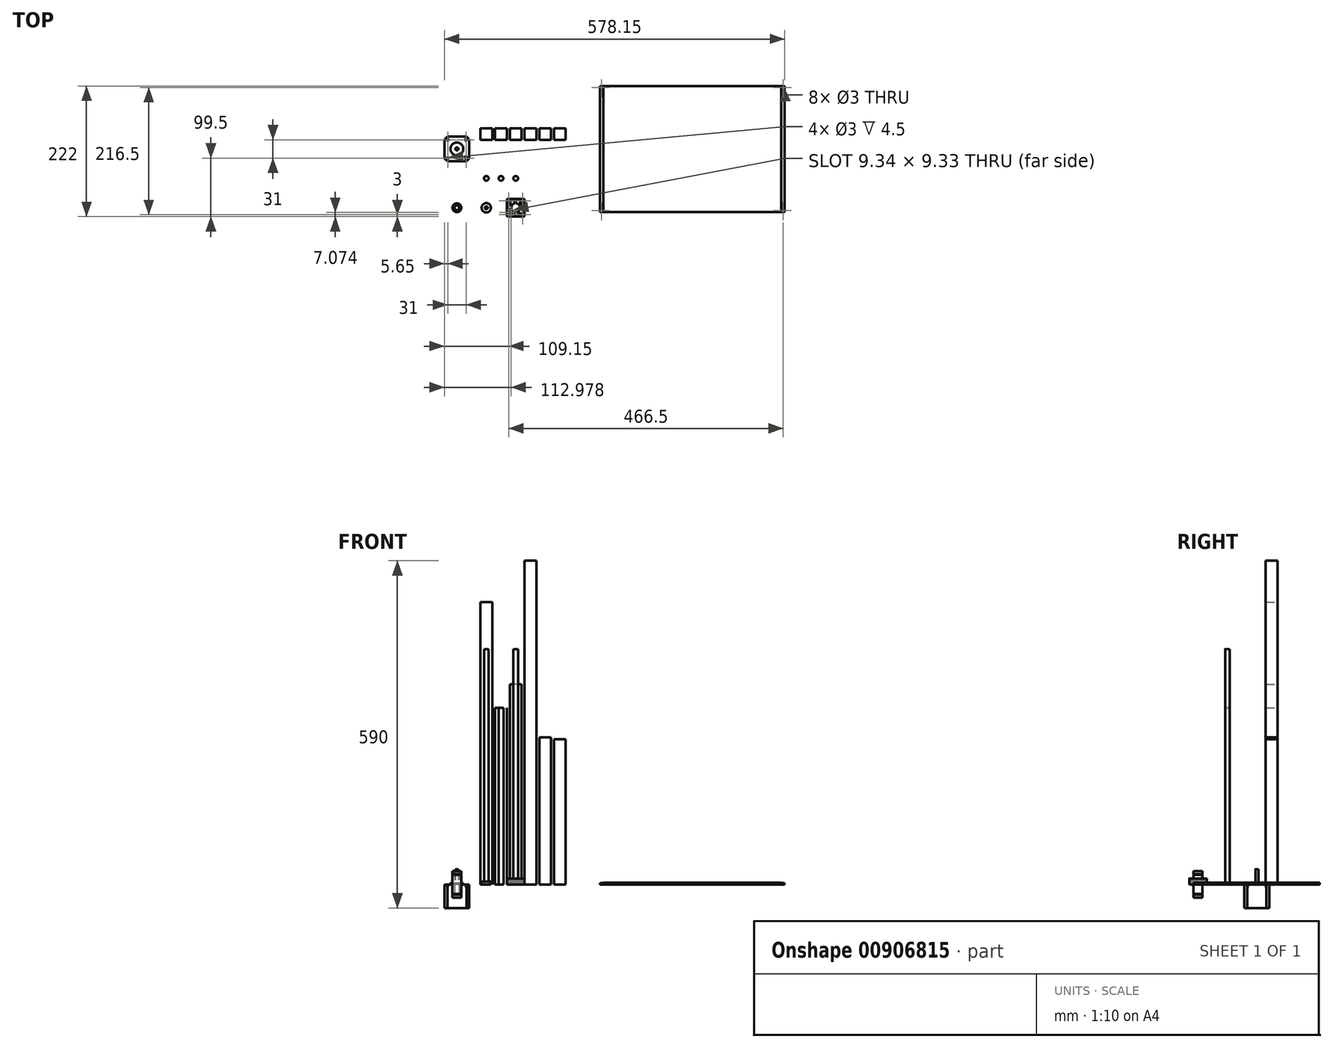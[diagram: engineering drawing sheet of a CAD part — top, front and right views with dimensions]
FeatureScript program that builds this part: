
annotation { "Feature Type Name" : "Feature", "Feature Type Description" : "" }
export const myFeature = defineFeature(function(context is Context, id is Id, definition is map)
    precondition{}
    {
        {
            assignVariable(context, id + "F0", {"name" : "X", "anyValue" : 480});
        }
        {
            assignVariable(context, id + "F1", {"name" : "Y", "anyValue" : 300});
        }
        {
            assignVariable(context, id + "F2", {"name" : "Z", "anyValue" : 550});
        }
        {
            var Q0;
            Q0=qCreatedBy(makeId("Top.planeOp"),FACE);
            var sketch = newSketch(context, id + "F3", { "sketchPlane" : qUnion([Q0])});
            skLineSegment(sketch, "E0.bottom", {"start": v(8.5, -10) * mm, "end": v(-8.5, -10) * mm});
            skLineSegment(sketch, "E0.top", {"start": v(8.5, 10) * mm, "end": v(-8.5, 10) * mm});
            skLineSegment(sketch, "E0.left", {"start": v(10, -8.5) * mm, "end": v(10, 8.5) * mm});
            skLineSegment(sketch, "E0.right", {"start": v(-10, -8.5) * mm, "end": v(-10, 8.5) * mm});
            skPoint(sketch, "E0.middle", {"position": v(0, 0) * mm});
            skPoint(sketch, "E1.visualSharp", {"position": v(-10, 10) * mm});
            skArc(sketch, "E1.filletArc", {"start": v(-8.5, 10) * mm, "mid": v(-9.56, 9.56) * mm, "end": v(-10, 8.5) * mm});
            skPoint(sketch, "E2.visualSharp", {"position": v(10, 10) * mm});
            skArc(sketch, "E2.filletArc", {"start": v(10, 8.5) * mm, "mid": v(9.56, 9.56) * mm, "end": v(8.5, 10) * mm});
            skPoint(sketch, "E3.visualSharp", {"position": v(10, -10) * mm});
            skArc(sketch, "E3.filletArc", {"start": v(8.5, -10) * mm, "mid": v(9.56, -9.56) * mm, "end": v(10, -8.5) * mm});
            skPoint(sketch, "E4.visualSharp", {"position": v(-10, -10) * mm});
            skArc(sketch, "E4.filletArc", {"start": v(-10, -8.5) * mm, "mid": v(-9.56, -9.56) * mm, "end": v(-8.5, -10) * mm});
            skCircle(sketch, "E5", {"center": v(0, 0) * mm, "radius": 2.5 * mm});
            skLineSegment(sketch, "E6", {"start": v(-3.6, -10) * mm, "end": v(-3.6, -9.7) * mm});
            skLineSegment(sketch, "E7", {"start": v(-3.4, -9.5) * mm, "end": v(-3.1, -9.5) * mm});
            skLineSegment(sketch, "E8", {"start": v(-3.1, -9.5) * mm, "end": v(-3.1, -8.2) * mm});
            skLineSegment(sketch, "E9", {"start": v(-3.1, -8.2) * mm, "end": v(-5.5, -8.2) * mm});
            skLineSegment(sketch, "E10", {"start": v(-3.43, -4.49) * mm, "end": v(-5.5, -6.56) * mm});
            skLineSegment(sketch, "E11", {"start": v(-2.01, -3.9) * mm, "end": v(2.01, -3.9) * mm});
            skLineSegment(sketch, "E12", {"start": v(5.5, -6.56) * mm, "end": v(3.43, -4.49) * mm});
            skLineSegment(sketch, "E13", {"start": v(5.5, -8.2) * mm, "end": v(3.1, -8.2) * mm});
            skLineSegment(sketch, "E14", {"start": v(3.1, -8.2) * mm, "end": v(3.1, -9.5) * mm});
            skLineSegment(sketch, "E15", {"start": v(3.1, -9.5) * mm, "end": v(3.4, -9.5) * mm});
            skLineSegment(sketch, "E16", {"start": v(3.6, -9.7) * mm, "end": v(3.6, -10) * mm});
            skLineSegment(sketch, "E17", {"start": v(0, 0) * mm, "end": v(0, -10) * mm, "construction": true});
            skLineSegment(sketch, "E18", {"start": v(5.5, -6.56) * mm, "end": v(5.5, -8.2) * mm});
            skLineSegment(sketch, "E19", {"start": v(-5.5, -6.56) * mm, "end": v(-5.5, -8.2) * mm});
            skPoint(sketch, "E20.visualSharp", {"position": v(-2.84, -3.9) * mm});
            skArc(sketch, "E20.filletArc", {"start": v(-2.01, -3.9) * mm, "mid": v(-2.78, -4.05) * mm, "end": v(-3.43, -4.49) * mm});
            skPoint(sketch, "E21.visualSharp", {"position": v(2.84, -3.9) * mm});
            skArc(sketch, "E21.filletArc", {"start": v(3.43, -4.49) * mm, "mid": v(2.78, -4.05) * mm, "end": v(2.01, -3.9) * mm});
            skPoint(sketch, "E22.visualSharp", {"position": v(-3.6, -9.5) * mm});
            skArc(sketch, "E22.filletArc", {"start": v(-3.4, -9.5) * mm, "mid": v(-3.54, -9.56) * mm, "end": v(-3.6, -9.7) * mm});
            skPoint(sketch, "E23.visualSharp", {"position": v(3.6, -9.5) * mm});
            skArc(sketch, "E23.filletArc", {"start": v(3.6, -9.7) * mm, "mid": v(3.54, -9.56) * mm, "end": v(3.4, -9.5) * mm});
            skLineSegment(sketch, "E24.1.0", {"start": v(6.56, 5.5) * mm, "end": v(4.49, 3.43) * mm});
            skLineSegment(sketch, "E24.1.1", {"start": v(3.9, -2.01) * mm, "end": v(3.9, 2.01) * mm});
            skLineSegment(sketch, "E24.1.2", {"start": v(6.56, 5.5) * mm, "end": v(8.2, 5.5) * mm});
            skArc(sketch, "E24.1.3", {"start": v(4.49, 3.43) * mm, "mid": v(4.05, 2.78) * mm, "end": v(3.9, 2.01) * mm});
            skLineSegment(sketch, "E24.1.4", {"start": v(8.2, 3.1) * mm, "end": v(9.5, 3.1) * mm});
            skPoint(sketch, "E24.1.5", {"position": v(3.9, -2.84) * mm});
            skPoint(sketch, "E24.1.6", {"position": v(9.5, -3.6) * mm});
            skPoint(sketch, "E24.1.7", {"position": v(9.5, 3.6) * mm});
            skLineSegment(sketch, "E24.1.8", {"start": v(8.2, -3.1) * mm, "end": v(8.2, -5.5) * mm});
            skLineSegment(sketch, "E24.1.9", {"start": v(9.7, 3.6) * mm, "end": v(10, 3.6) * mm});
            skLineSegment(sketch, "E24.1.10", {"start": v(9.5, -3.1) * mm, "end": v(8.2, -3.1) * mm});
            skLineSegment(sketch, "E24.1.11", {"start": v(8.2, 5.5) * mm, "end": v(8.2, 3.1) * mm});
            skLineSegment(sketch, "E24.1.12", {"start": v(4.49, -3.43) * mm, "end": v(6.56, -5.5) * mm});
            skPoint(sketch, "E24.1.13", {"position": v(3.9, 2.84) * mm});
            skLineSegment(sketch, "E24.1.14", {"start": v(6.56, -5.5) * mm, "end": v(8.2, -5.5) * mm});
            skLineSegment(sketch, "E24.1.15", {"start": v(9.5, 3.1) * mm, "end": v(9.5, 3.4) * mm});
            skLineSegment(sketch, "E24.1.16", {"start": v(9.5, -3.4) * mm, "end": v(9.5, -3.1) * mm});
            skArc(sketch, "E24.1.17", {"start": v(3.9, -2.01) * mm, "mid": v(4.05, -2.78) * mm, "end": v(4.49, -3.43) * mm});
            skLineSegment(sketch, "E24.1.18", {"start": v(10, -3.6) * mm, "end": v(9.7, -3.6) * mm});
            skArc(sketch, "E24.1.19", {"start": v(9.5, -3.4) * mm, "mid": v(9.56, -3.54) * mm, "end": v(9.7, -3.6) * mm});
            skArc(sketch, "E24.1.20", {"start": v(9.7, 3.6) * mm, "mid": v(9.56, 3.54) * mm, "end": v(9.5, 3.4) * mm});
            skLineSegment(sketch, "E24.2.0", {"start": v(-5.5, 6.56) * mm, "end": v(-3.43, 4.49) * mm});
            skLineSegment(sketch, "E24.2.1", {"start": v(2.01, 3.9) * mm, "end": v(-2.01, 3.9) * mm});
            skLineSegment(sketch, "E24.2.2", {"start": v(-5.5, 6.56) * mm, "end": v(-5.5, 8.2) * mm});
            skArc(sketch, "E24.2.3", {"start": v(-3.43, 4.49) * mm, "mid": v(-2.78, 4.05) * mm, "end": v(-2.01, 3.9) * mm});
            skLineSegment(sketch, "E24.2.4", {"start": v(-3.1, 8.2) * mm, "end": v(-3.1, 9.5) * mm});
            skPoint(sketch, "E24.2.5", {"position": v(2.84, 3.9) * mm});
            skPoint(sketch, "E24.2.6", {"position": v(3.6, 9.5) * mm});
            skPoint(sketch, "E24.2.7", {"position": v(-3.6, 9.5) * mm});
            skLineSegment(sketch, "E24.2.8", {"start": v(3.1, 8.2) * mm, "end": v(5.5, 8.2) * mm});
            skLineSegment(sketch, "E24.2.9", {"start": v(-3.6, 9.7) * mm, "end": v(-3.6, 10) * mm});
            skLineSegment(sketch, "E24.2.10", {"start": v(3.1, 9.5) * mm, "end": v(3.1, 8.2) * mm});
            skLineSegment(sketch, "E24.2.11", {"start": v(-5.5, 8.2) * mm, "end": v(-3.1, 8.2) * mm});
            skLineSegment(sketch, "E24.2.12", {"start": v(3.43, 4.49) * mm, "end": v(5.5, 6.56) * mm});
            skPoint(sketch, "E24.2.13", {"position": v(-2.84, 3.9) * mm});
            skLineSegment(sketch, "E24.2.14", {"start": v(5.5, 6.56) * mm, "end": v(5.5, 8.2) * mm});
            skLineSegment(sketch, "E24.2.15", {"start": v(-3.1, 9.5) * mm, "end": v(-3.4, 9.5) * mm});
            skLineSegment(sketch, "E24.2.16", {"start": v(3.4, 9.5) * mm, "end": v(3.1, 9.5) * mm});
            skArc(sketch, "E24.2.17", {"start": v(2.01, 3.9) * mm, "mid": v(2.78, 4.05) * mm, "end": v(3.43, 4.49) * mm});
            skLineSegment(sketch, "E24.2.18", {"start": v(3.6, 10) * mm, "end": v(3.6, 9.7) * mm});
            skArc(sketch, "E24.2.19", {"start": v(3.4, 9.5) * mm, "mid": v(3.54, 9.56) * mm, "end": v(3.6, 9.7) * mm});
            skArc(sketch, "E24.2.20", {"start": v(-3.6, 9.7) * mm, "mid": v(-3.54, 9.56) * mm, "end": v(-3.4, 9.5) * mm});
            skLineSegment(sketch, "E24.3.0", {"start": v(-6.56, -5.5) * mm, "end": v(-4.49, -3.43) * mm});
            skLineSegment(sketch, "E24.3.1", {"start": v(-3.9, 2.01) * mm, "end": v(-3.9, -2.01) * mm});
            skLineSegment(sketch, "E24.3.2", {"start": v(-6.56, -5.5) * mm, "end": v(-8.2, -5.5) * mm});
            skArc(sketch, "E24.3.3", {"start": v(-4.49, -3.43) * mm, "mid": v(-4.05, -2.78) * mm, "end": v(-3.9, -2.01) * mm});
            skLineSegment(sketch, "E24.3.4", {"start": v(-8.2, -3.1) * mm, "end": v(-9.5, -3.1) * mm});
            skPoint(sketch, "E24.3.5", {"position": v(-3.9, 2.84) * mm});
            skPoint(sketch, "E24.3.6", {"position": v(-9.5, 3.6) * mm});
            skPoint(sketch, "E24.3.7", {"position": v(-9.5, -3.6) * mm});
            skLineSegment(sketch, "E24.3.8", {"start": v(-8.2, 3.1) * mm, "end": v(-8.2, 5.5) * mm});
            skLineSegment(sketch, "E24.3.9", {"start": v(-9.7, -3.6) * mm, "end": v(-10, -3.6) * mm});
            skLineSegment(sketch, "E24.3.10", {"start": v(-9.5, 3.1) * mm, "end": v(-8.2, 3.1) * mm});
            skLineSegment(sketch, "E24.3.11", {"start": v(-8.2, -5.5) * mm, "end": v(-8.2, -3.1) * mm});
            skLineSegment(sketch, "E24.3.12", {"start": v(-4.49, 3.43) * mm, "end": v(-6.56, 5.5) * mm});
            skPoint(sketch, "E24.3.13", {"position": v(-3.9, -2.84) * mm});
            skLineSegment(sketch, "E24.3.14", {"start": v(-6.56, 5.5) * mm, "end": v(-8.2, 5.5) * mm});
            skLineSegment(sketch, "E24.3.15", {"start": v(-9.5, -3.1) * mm, "end": v(-9.5, -3.4) * mm});
            skLineSegment(sketch, "E24.3.16", {"start": v(-9.5, 3.4) * mm, "end": v(-9.5, 3.1) * mm});
            skArc(sketch, "E24.3.17", {"start": v(-3.9, 2.01) * mm, "mid": v(-4.05, 2.78) * mm, "end": v(-4.49, 3.43) * mm});
            skLineSegment(sketch, "E24.3.18", {"start": v(-10, 3.6) * mm, "end": v(-9.7, 3.6) * mm});
            skArc(sketch, "E24.3.19", {"start": v(-9.5, 3.4) * mm, "mid": v(-9.56, 3.54) * mm, "end": v(-9.7, 3.6) * mm});
            skArc(sketch, "E24.3.20", {"start": v(-9.7, -3.6) * mm, "mid": v(-9.56, -3.54) * mm, "end": v(-9.5, -3.4) * mm});
            skLineSegment(sketch, "E25.1.0.0", {"start": v(33.5, 10) * mm, "end": v(16.5, 10) * mm});
            skLineSegment(sketch, "E25.1.0.1", {"start": v(35, -8.5) * mm, "end": v(35, 8.5) * mm});
            skLineSegment(sketch, "E25.1.0.2", {"start": v(33.5, -10) * mm, "end": v(16.5, -10) * mm});
            skLineSegment(sketch, "E25.1.0.3", {"start": v(30.5, -6.56) * mm, "end": v(28.43, -4.49) * mm});
            skLineSegment(sketch, "E25.1.0.4", {"start": v(15, -8.5) * mm, "end": v(15, 8.5) * mm});
            skPoint(sketch, "E25.1.0.5", {"position": v(15, 10) * mm});
            skPoint(sketch, "E25.1.0.6", {"position": v(35, -10) * mm});
            skCircle(sketch, "E25.1.0.7", {"center": v(25, 0) * mm, "radius": 2.5 * mm});
            skLineSegment(sketch, "E25.1.0.8", {"start": v(28.1, 8.2) * mm, "end": v(30.5, 8.2) * mm});
            skPoint(sketch, "E25.1.0.9", {"position": v(21.1, -2.84) * mm});
            skPoint(sketch, "E25.1.0.10", {"position": v(28.9, 2.84) * mm});
            skLineSegment(sketch, "E25.1.0.11", {"start": v(18.44, -5.5) * mm, "end": v(20.51, -3.43) * mm});
            skLineSegment(sketch, "E25.1.0.12", {"start": v(30.5, -8.2) * mm, "end": v(28.1, -8.2) * mm});
            skPoint(sketch, "E25.1.0.13", {"position": v(15, -10) * mm});
            skLineSegment(sketch, "E25.1.0.14", {"start": v(22.99, -3.9) * mm, "end": v(27.01, -3.9) * mm});
            skLineSegment(sketch, "E25.1.0.15", {"start": v(27.01, 3.9) * mm, "end": v(22.99, 3.9) * mm});
            skLineSegment(sketch, "E25.1.0.16", {"start": v(31.56, 5.5) * mm, "end": v(29.49, 3.43) * mm});
            skPoint(sketch, "E25.1.0.17", {"position": v(15.5, 3.6) * mm});
            skPoint(sketch, "E25.1.0.18", {"position": v(34.5, -3.6) * mm});
            skLineSegment(sketch, "E25.1.0.19", {"start": v(33.2, -3.1) * mm, "end": v(33.2, -5.5) * mm});
            skLineSegment(sketch, "E25.1.0.20", {"start": v(21.57, -4.49) * mm, "end": v(19.5, -6.56) * mm});
            skPoint(sketch, "E25.1.0.21", {"position": v(15.5, -3.6) * mm});
            skPoint(sketch, "E25.1.0.22", {"position": v(34.5, 3.6) * mm});
            skLineSegment(sketch, "E25.1.0.23", {"start": v(19.5, 6.56) * mm, "end": v(21.57, 4.49) * mm});
            skLineSegment(sketch, "E25.1.0.24", {"start": v(28.9, -2.01) * mm, "end": v(28.9, 2.01) * mm});
            skLineSegment(sketch, "E25.1.0.25", {"start": v(21.1, 2.01) * mm, "end": v(21.1, -2.01) * mm});
            skLineSegment(sketch, "E25.1.0.26", {"start": v(16.8, 3.1) * mm, "end": v(16.8, 5.5) * mm});
            skPoint(sketch, "E25.1.0.27", {"position": v(35, 10) * mm});
            skPoint(sketch, "E25.1.0.28", {"position": v(28.9, -2.84) * mm});
            skPoint(sketch, "E25.1.0.29", {"position": v(21.1, 2.84) * mm});
            skPoint(sketch, "E25.1.0.30", {"position": v(25, 0) * mm});
            skPoint(sketch, "E25.1.0.31", {"position": v(28.6, -9.5) * mm});
            skPoint(sketch, "E25.1.0.32", {"position": v(22.16, 3.9) * mm});
            skPoint(sketch, "E25.1.0.33", {"position": v(21.4, 9.5) * mm});
            skLineSegment(sketch, "E25.1.0.34", {"start": v(20.51, 3.43) * mm, "end": v(18.44, 5.5) * mm});
            skPoint(sketch, "E25.1.0.35", {"position": v(27.84, -3.9) * mm});
            skPoint(sketch, "E25.1.0.36", {"position": v(28.6, 9.5) * mm});
            skLineSegment(sketch, "E25.1.0.37", {"start": v(28.43, 4.49) * mm, "end": v(30.5, 6.56) * mm});
            skLineSegment(sketch, "E25.1.0.38", {"start": v(16.8, -5.5) * mm, "end": v(16.8, -3.1) * mm});
            skPoint(sketch, "E25.1.0.39", {"position": v(27.84, 3.9) * mm});
            skLineSegment(sketch, "E25.1.0.40", {"start": v(29.49, -3.43) * mm, "end": v(31.56, -5.5) * mm});
            skLineSegment(sketch, "E25.1.0.41", {"start": v(19.5, 8.2) * mm, "end": v(21.9, 8.2) * mm});
            skLineSegment(sketch, "E25.1.0.42", {"start": v(25, 0) * mm, "end": v(25, -10) * mm, "construction": true});
            skPoint(sketch, "E25.1.0.43", {"position": v(22.16, -3.9) * mm});
            skLineSegment(sketch, "E25.1.0.44", {"start": v(33.2, 5.5) * mm, "end": v(33.2, 3.1) * mm});
            skArc(sketch, "E25.1.0.45", {"start": v(35, 8.5) * mm, "mid": v(34.56, 9.56) * mm, "end": v(33.5, 10) * mm});
            skArc(sketch, "E25.1.0.46", {"start": v(16.5, 10) * mm, "mid": v(15.44, 9.56) * mm, "end": v(15, 8.5) * mm});
            skLineSegment(sketch, "E25.1.0.47", {"start": v(21.9, -8.2) * mm, "end": v(19.5, -8.2) * mm});
            skArc(sketch, "E25.1.0.48", {"start": v(33.5, -10) * mm, "mid": v(34.56, -9.56) * mm, "end": v(35, -8.5) * mm});
            skArc(sketch, "E25.1.0.49", {"start": v(15, -8.5) * mm, "mid": v(15.44, -9.56) * mm, "end": v(16.5, -10) * mm});
            skPoint(sketch, "E25.1.0.50", {"position": v(21.4, -9.5) * mm});
            skPoint(sketch, "E25.1.0.51", {"position": v(25, 0) * mm});
            skLineSegment(sketch, "E25.1.0.52", {"start": v(28.1, -8.2) * mm, "end": v(28.1, -9.5) * mm});
            skLineSegment(sketch, "E25.1.0.53", {"start": v(16.8, -3.1) * mm, "end": v(15.5, -3.1) * mm});
            skLineSegment(sketch, "E25.1.0.54", {"start": v(18.44, -5.5) * mm, "end": v(16.8, -5.5) * mm});
            skArc(sketch, "E25.1.0.55", {"start": v(20.51, -3.43) * mm, "mid": v(20.95, -2.78) * mm, "end": v(21.1, -2.01) * mm});
            skLineSegment(sketch, "E25.1.0.56", {"start": v(21.9, 8.2) * mm, "end": v(21.9, 9.5) * mm});
            skLineSegment(sketch, "E25.1.0.57", {"start": v(33.2, 3.1) * mm, "end": v(34.5, 3.1) * mm});
            skLineSegment(sketch, "E25.1.0.58", {"start": v(31.56, 5.5) * mm, "end": v(33.2, 5.5) * mm});
            skArc(sketch, "E25.1.0.59", {"start": v(21.57, 4.49) * mm, "mid": v(22.22, 4.05) * mm, "end": v(22.99, 3.9) * mm});
            skLineSegment(sketch, "E25.1.0.60", {"start": v(19.5, 6.56) * mm, "end": v(19.5, 8.2) * mm});
            skLineSegment(sketch, "E25.1.0.61", {"start": v(34.5, -3.1) * mm, "end": v(33.2, -3.1) * mm});
            skArc(sketch, "E25.1.0.62", {"start": v(29.49, 3.43) * mm, "mid": v(29.05, 2.78) * mm, "end": v(28.9, 2.01) * mm});
            skArc(sketch, "E25.1.0.63", {"start": v(21.1, 2.01) * mm, "mid": v(20.95, 2.78) * mm, "end": v(20.51, 3.43) * mm});
            skArc(sketch, "E25.1.0.64", {"start": v(27.01, 3.9) * mm, "mid": v(27.78, 4.05) * mm, "end": v(28.43, 4.49) * mm});
            skArc(sketch, "E25.1.0.65", {"start": v(28.43, -4.49) * mm, "mid": v(27.78, -4.05) * mm, "end": v(27.01, -3.9) * mm});
            skArc(sketch, "E25.1.0.66", {"start": v(28.9, -2.01) * mm, "mid": v(29.05, -2.78) * mm, "end": v(29.49, -3.43) * mm});
            skLineSegment(sketch, "E25.1.0.67", {"start": v(18.44, 5.5) * mm, "end": v(16.8, 5.5) * mm});
            skArc(sketch, "E25.1.0.68", {"start": v(22.99, -3.9) * mm, "mid": v(22.22, -4.05) * mm, "end": v(21.57, -4.49) * mm});
            skLineSegment(sketch, "E25.1.0.69", {"start": v(30.5, 6.56) * mm, "end": v(30.5, 8.2) * mm});
            skLineSegment(sketch, "E25.1.0.70", {"start": v(19.5, -6.56) * mm, "end": v(19.5, -8.2) * mm});
            skLineSegment(sketch, "E25.1.0.71", {"start": v(31.56, -5.5) * mm, "end": v(33.2, -5.5) * mm});
            skLineSegment(sketch, "E25.1.0.72", {"start": v(30.5, -6.56) * mm, "end": v(30.5, -8.2) * mm});
            skLineSegment(sketch, "E25.1.0.73", {"start": v(15.5, 3.1) * mm, "end": v(16.8, 3.1) * mm});
            skLineSegment(sketch, "E25.1.0.74", {"start": v(28.1, 9.5) * mm, "end": v(28.1, 8.2) * mm});
            skLineSegment(sketch, "E25.1.0.75", {"start": v(21.9, -9.5) * mm, "end": v(21.9, -8.2) * mm});
            skArc(sketch, "E25.1.0.76", {"start": v(34.5, -3.4) * mm, "mid": v(34.56, -3.54) * mm, "end": v(34.7, -3.6) * mm});
            skLineSegment(sketch, "E25.1.0.77", {"start": v(35, -3.6) * mm, "end": v(34.7, -3.6) * mm});
            skLineSegment(sketch, "E25.1.0.78", {"start": v(34.5, -3.4) * mm, "end": v(34.5, -3.1) * mm});
            skArc(sketch, "E25.1.0.79", {"start": v(15.3, -3.6) * mm, "mid": v(15.44, -3.54) * mm, "end": v(15.5, -3.4) * mm});
            skArc(sketch, "E25.1.0.80", {"start": v(28.4, 9.5) * mm, "mid": v(28.54, 9.56) * mm, "end": v(28.6, 9.7) * mm});
            skLineSegment(sketch, "E25.1.0.81", {"start": v(28.1, -9.5) * mm, "end": v(28.4, -9.5) * mm});
            skArc(sketch, "E25.1.0.82", {"start": v(28.6, -9.7) * mm, "mid": v(28.54, -9.56) * mm, "end": v(28.4, -9.5) * mm});
            skLineSegment(sketch, "E25.1.0.83", {"start": v(28.6, 10) * mm, "end": v(28.6, 9.7) * mm});
            skLineSegment(sketch, "E25.1.0.84", {"start": v(15.5, -3.1) * mm, "end": v(15.5, -3.4) * mm});
            skLineSegment(sketch, "E25.1.0.85", {"start": v(28.4, 9.5) * mm, "end": v(28.1, 9.5) * mm});
            skLineSegment(sketch, "E25.1.0.86", {"start": v(15.3, -3.6) * mm, "end": v(15, -3.6) * mm});
            skLineSegment(sketch, "E25.1.0.87", {"start": v(28.6, -9.7) * mm, "end": v(28.6, -10) * mm});
            skArc(sketch, "E25.1.0.88", {"start": v(21.4, 9.7) * mm, "mid": v(21.46, 9.56) * mm, "end": v(21.6, 9.5) * mm});
            skLineSegment(sketch, "E25.1.0.89", {"start": v(21.4, -10) * mm, "end": v(21.4, -9.7) * mm});
            skLineSegment(sketch, "E25.1.0.90", {"start": v(21.6, -9.5) * mm, "end": v(21.9, -9.5) * mm});
            skLineSegment(sketch, "E25.1.0.91", {"start": v(21.4, 9.7) * mm, "end": v(21.4, 10) * mm});
            skLineSegment(sketch, "E25.1.0.92", {"start": v(21.9, 9.5) * mm, "end": v(21.6, 9.5) * mm});
            skLineSegment(sketch, "E25.1.0.93", {"start": v(15, 3.6) * mm, "end": v(15.3, 3.6) * mm});
            skArc(sketch, "E25.1.0.94", {"start": v(34.7, 3.6) * mm, "mid": v(34.56, 3.54) * mm, "end": v(34.5, 3.4) * mm});
            skArc(sketch, "E25.1.0.95", {"start": v(15.5, 3.4) * mm, "mid": v(15.44, 3.54) * mm, "end": v(15.3, 3.6) * mm});
            skLineSegment(sketch, "E25.1.0.96", {"start": v(34.7, 3.6) * mm, "end": v(35, 3.6) * mm});
            skLineSegment(sketch, "E25.1.0.97", {"start": v(15.5, 3.4) * mm, "end": v(15.5, 3.1) * mm});
            skArc(sketch, "E25.1.0.98", {"start": v(21.6, -9.5) * mm, "mid": v(21.46, -9.56) * mm, "end": v(21.4, -9.7) * mm});
            skLineSegment(sketch, "E25.1.0.99", {"start": v(34.5, 3.1) * mm, "end": v(34.5, 3.4) * mm});
            skLineSegment(sketch, "E25.2.0.0", {"start": v(58.5, 10) * mm, "end": v(41.5, 10) * mm});
            skLineSegment(sketch, "E25.2.0.1", {"start": v(60, -8.5) * mm, "end": v(60, 8.5) * mm});
            skLineSegment(sketch, "E25.2.0.2", {"start": v(58.5, -10) * mm, "end": v(41.5, -10) * mm});
            skLineSegment(sketch, "E25.2.0.3", {"start": v(55.5, -6.56) * mm, "end": v(53.43, -4.49) * mm});
            skLineSegment(sketch, "E25.2.0.4", {"start": v(40, -8.5) * mm, "end": v(40, 8.5) * mm});
            skPoint(sketch, "E25.2.0.5", {"position": v(40, 10) * mm});
            skPoint(sketch, "E25.2.0.6", {"position": v(60, -10) * mm});
            skCircle(sketch, "E25.2.0.7", {"center": v(50, 0) * mm, "radius": 2.5 * mm});
            skLineSegment(sketch, "E25.2.0.8", {"start": v(53.1, 8.2) * mm, "end": v(55.5, 8.2) * mm});
            skPoint(sketch, "E25.2.0.9", {"position": v(46.1, -2.84) * mm});
            skPoint(sketch, "E25.2.0.10", {"position": v(53.9, 2.84) * mm});
            skLineSegment(sketch, "E25.2.0.11", {"start": v(43.44, -5.5) * mm, "end": v(45.51, -3.43) * mm});
            skLineSegment(sketch, "E25.2.0.12", {"start": v(55.5, -8.2) * mm, "end": v(53.1, -8.2) * mm});
            skPoint(sketch, "E25.2.0.13", {"position": v(40, -10) * mm});
            skLineSegment(sketch, "E25.2.0.14", {"start": v(47.99, -3.9) * mm, "end": v(52.01, -3.9) * mm});
            skLineSegment(sketch, "E25.2.0.15", {"start": v(52.01, 3.9) * mm, "end": v(47.99, 3.9) * mm});
            skLineSegment(sketch, "E25.2.0.16", {"start": v(56.56, 5.5) * mm, "end": v(54.49, 3.43) * mm});
            skPoint(sketch, "E25.2.0.17", {"position": v(40.5, 3.6) * mm});
            skPoint(sketch, "E25.2.0.18", {"position": v(59.5, -3.6) * mm});
            skLineSegment(sketch, "E25.2.0.19", {"start": v(58.2, -3.1) * mm, "end": v(58.2, -5.5) * mm});
            skLineSegment(sketch, "E25.2.0.20", {"start": v(46.57, -4.49) * mm, "end": v(44.5, -6.56) * mm});
            skPoint(sketch, "E25.2.0.21", {"position": v(40.5, -3.6) * mm});
            skPoint(sketch, "E25.2.0.22", {"position": v(59.5, 3.6) * mm});
            skLineSegment(sketch, "E25.2.0.23", {"start": v(44.5, 6.56) * mm, "end": v(46.57, 4.49) * mm});
            skLineSegment(sketch, "E25.2.0.24", {"start": v(53.9, -2.01) * mm, "end": v(53.9, 2.01) * mm});
            skLineSegment(sketch, "E25.2.0.25", {"start": v(46.1, 2.01) * mm, "end": v(46.1, -2.01) * mm});
            skLineSegment(sketch, "E25.2.0.26", {"start": v(41.8, 3.1) * mm, "end": v(41.8, 5.5) * mm});
            skPoint(sketch, "E25.2.0.27", {"position": v(60, 10) * mm});
            skPoint(sketch, "E25.2.0.28", {"position": v(53.9, -2.84) * mm});
            skPoint(sketch, "E25.2.0.29", {"position": v(46.1, 2.84) * mm});
            skPoint(sketch, "E25.2.0.30", {"position": v(50, 0) * mm});
            skPoint(sketch, "E25.2.0.31", {"position": v(53.6, -9.5) * mm});
            skPoint(sketch, "E25.2.0.32", {"position": v(47.16, 3.9) * mm});
            skPoint(sketch, "E25.2.0.33", {"position": v(46.4, 9.5) * mm});
            skLineSegment(sketch, "E25.2.0.34", {"start": v(45.51, 3.43) * mm, "end": v(43.44, 5.5) * mm});
            skPoint(sketch, "E25.2.0.35", {"position": v(52.84, -3.9) * mm});
            skPoint(sketch, "E25.2.0.36", {"position": v(53.6, 9.5) * mm});
            skLineSegment(sketch, "E25.2.0.37", {"start": v(53.43, 4.49) * mm, "end": v(55.5, 6.56) * mm});
            skLineSegment(sketch, "E25.2.0.38", {"start": v(41.8, -5.5) * mm, "end": v(41.8, -3.1) * mm});
            skPoint(sketch, "E25.2.0.39", {"position": v(52.84, 3.9) * mm});
            skLineSegment(sketch, "E25.2.0.40", {"start": v(54.49, -3.43) * mm, "end": v(56.56, -5.5) * mm});
            skLineSegment(sketch, "E25.2.0.41", {"start": v(44.5, 8.2) * mm, "end": v(46.9, 8.2) * mm});
            skLineSegment(sketch, "E25.2.0.42", {"start": v(50, 0) * mm, "end": v(50, -10) * mm, "construction": true});
            skPoint(sketch, "E25.2.0.43", {"position": v(47.16, -3.9) * mm});
            skLineSegment(sketch, "E25.2.0.44", {"start": v(58.2, 5.5) * mm, "end": v(58.2, 3.1) * mm});
            skArc(sketch, "E25.2.0.45", {"start": v(60, 8.5) * mm, "mid": v(59.56, 9.56) * mm, "end": v(58.5, 10) * mm});
            skArc(sketch, "E25.2.0.46", {"start": v(41.5, 10) * mm, "mid": v(40.44, 9.56) * mm, "end": v(40, 8.5) * mm});
            skLineSegment(sketch, "E25.2.0.47", {"start": v(46.9, -8.2) * mm, "end": v(44.5, -8.2) * mm});
            skArc(sketch, "E25.2.0.48", {"start": v(58.5, -10) * mm, "mid": v(59.56, -9.56) * mm, "end": v(60, -8.5) * mm});
            skArc(sketch, "E25.2.0.49", {"start": v(40, -8.5) * mm, "mid": v(40.44, -9.56) * mm, "end": v(41.5, -10) * mm});
            skPoint(sketch, "E25.2.0.50", {"position": v(46.4, -9.5) * mm});
            skPoint(sketch, "E25.2.0.51", {"position": v(50, 0) * mm});
            skLineSegment(sketch, "E25.2.0.52", {"start": v(53.1, -8.2) * mm, "end": v(53.1, -9.5) * mm});
            skLineSegment(sketch, "E25.2.0.53", {"start": v(41.8, -3.1) * mm, "end": v(40.5, -3.1) * mm});
            skLineSegment(sketch, "E25.2.0.54", {"start": v(43.44, -5.5) * mm, "end": v(41.8, -5.5) * mm});
            skArc(sketch, "E25.2.0.55", {"start": v(45.51, -3.43) * mm, "mid": v(45.95, -2.78) * mm, "end": v(46.1, -2.01) * mm});
            skLineSegment(sketch, "E25.2.0.56", {"start": v(46.9, 8.2) * mm, "end": v(46.9, 9.5) * mm});
            skLineSegment(sketch, "E25.2.0.57", {"start": v(58.2, 3.1) * mm, "end": v(59.5, 3.1) * mm});
            skLineSegment(sketch, "E25.2.0.58", {"start": v(56.56, 5.5) * mm, "end": v(58.2, 5.5) * mm});
            skArc(sketch, "E25.2.0.59", {"start": v(46.57, 4.49) * mm, "mid": v(47.22, 4.05) * mm, "end": v(47.99, 3.9) * mm});
            skLineSegment(sketch, "E25.2.0.60", {"start": v(44.5, 6.56) * mm, "end": v(44.5, 8.2) * mm});
            skLineSegment(sketch, "E25.2.0.61", {"start": v(59.5, -3.1) * mm, "end": v(58.2, -3.1) * mm});
            skArc(sketch, "E25.2.0.62", {"start": v(54.49, 3.43) * mm, "mid": v(54.05, 2.78) * mm, "end": v(53.9, 2.01) * mm});
            skArc(sketch, "E25.2.0.63", {"start": v(46.1, 2.01) * mm, "mid": v(45.95, 2.78) * mm, "end": v(45.51, 3.43) * mm});
            skArc(sketch, "E25.2.0.64", {"start": v(52.01, 3.9) * mm, "mid": v(52.78, 4.05) * mm, "end": v(53.43, 4.49) * mm});
            skArc(sketch, "E25.2.0.65", {"start": v(53.43, -4.49) * mm, "mid": v(52.78, -4.05) * mm, "end": v(52.01, -3.9) * mm});
            skArc(sketch, "E25.2.0.66", {"start": v(53.9, -2.01) * mm, "mid": v(54.05, -2.78) * mm, "end": v(54.49, -3.43) * mm});
            skLineSegment(sketch, "E25.2.0.67", {"start": v(43.44, 5.5) * mm, "end": v(41.8, 5.5) * mm});
            skArc(sketch, "E25.2.0.68", {"start": v(47.99, -3.9) * mm, "mid": v(47.22, -4.05) * mm, "end": v(46.57, -4.49) * mm});
            skLineSegment(sketch, "E25.2.0.69", {"start": v(55.5, 6.56) * mm, "end": v(55.5, 8.2) * mm});
            skLineSegment(sketch, "E25.2.0.70", {"start": v(44.5, -6.56) * mm, "end": v(44.5, -8.2) * mm});
            skLineSegment(sketch, "E25.2.0.71", {"start": v(56.56, -5.5) * mm, "end": v(58.2, -5.5) * mm});
            skLineSegment(sketch, "E25.2.0.72", {"start": v(55.5, -6.56) * mm, "end": v(55.5, -8.2) * mm});
            skLineSegment(sketch, "E25.2.0.73", {"start": v(40.5, 3.1) * mm, "end": v(41.8, 3.1) * mm});
            skLineSegment(sketch, "E25.2.0.74", {"start": v(53.1, 9.5) * mm, "end": v(53.1, 8.2) * mm});
            skLineSegment(sketch, "E25.2.0.75", {"start": v(46.9, -9.5) * mm, "end": v(46.9, -8.2) * mm});
            skArc(sketch, "E25.2.0.76", {"start": v(59.5, -3.4) * mm, "mid": v(59.56, -3.54) * mm, "end": v(59.7, -3.6) * mm});
            skLineSegment(sketch, "E25.2.0.77", {"start": v(60, -3.6) * mm, "end": v(59.7, -3.6) * mm});
            skLineSegment(sketch, "E25.2.0.78", {"start": v(59.5, -3.4) * mm, "end": v(59.5, -3.1) * mm});
            skArc(sketch, "E25.2.0.79", {"start": v(40.3, -3.6) * mm, "mid": v(40.44, -3.54) * mm, "end": v(40.5, -3.4) * mm});
            skArc(sketch, "E25.2.0.80", {"start": v(53.4, 9.5) * mm, "mid": v(53.54, 9.56) * mm, "end": v(53.6, 9.7) * mm});
            skLineSegment(sketch, "E25.2.0.81", {"start": v(53.1, -9.5) * mm, "end": v(53.4, -9.5) * mm});
            skArc(sketch, "E25.2.0.82", {"start": v(53.6, -9.7) * mm, "mid": v(53.54, -9.56) * mm, "end": v(53.4, -9.5) * mm});
            skLineSegment(sketch, "E25.2.0.83", {"start": v(53.6, 10) * mm, "end": v(53.6, 9.7) * mm});
            skLineSegment(sketch, "E25.2.0.84", {"start": v(40.5, -3.1) * mm, "end": v(40.5, -3.4) * mm});
            skLineSegment(sketch, "E25.2.0.85", {"start": v(53.4, 9.5) * mm, "end": v(53.1, 9.5) * mm});
            skLineSegment(sketch, "E25.2.0.86", {"start": v(40.3, -3.6) * mm, "end": v(40, -3.6) * mm});
            skLineSegment(sketch, "E25.2.0.87", {"start": v(53.6, -9.7) * mm, "end": v(53.6, -10) * mm});
            skArc(sketch, "E25.2.0.88", {"start": v(46.4, 9.7) * mm, "mid": v(46.46, 9.56) * mm, "end": v(46.6, 9.5) * mm});
            skLineSegment(sketch, "E25.2.0.89", {"start": v(46.4, -10) * mm, "end": v(46.4, -9.7) * mm});
            skLineSegment(sketch, "E25.2.0.90", {"start": v(46.6, -9.5) * mm, "end": v(46.9, -9.5) * mm});
            skLineSegment(sketch, "E25.2.0.91", {"start": v(46.4, 9.7) * mm, "end": v(46.4, 10) * mm});
            skLineSegment(sketch, "E25.2.0.92", {"start": v(46.9, 9.5) * mm, "end": v(46.6, 9.5) * mm});
            skLineSegment(sketch, "E25.2.0.93", {"start": v(40, 3.6) * mm, "end": v(40.3, 3.6) * mm});
            skArc(sketch, "E25.2.0.94", {"start": v(59.7, 3.6) * mm, "mid": v(59.56, 3.54) * mm, "end": v(59.5, 3.4) * mm});
            skArc(sketch, "E25.2.0.95", {"start": v(40.5, 3.4) * mm, "mid": v(40.44, 3.54) * mm, "end": v(40.3, 3.6) * mm});
            skLineSegment(sketch, "E25.2.0.96", {"start": v(59.7, 3.6) * mm, "end": v(60, 3.6) * mm});
            skLineSegment(sketch, "E25.2.0.97", {"start": v(40.5, 3.4) * mm, "end": v(40.5, 3.1) * mm});
            skArc(sketch, "E25.2.0.98", {"start": v(46.6, -9.5) * mm, "mid": v(46.46, -9.56) * mm, "end": v(46.4, -9.7) * mm});
            skLineSegment(sketch, "E25.2.0.99", {"start": v(59.5, 3.1) * mm, "end": v(59.5, 3.4) * mm});
            skLineSegment(sketch, "E25.direction1", {"start": v(-10, -10) * mm, "end": v(15, -10) * mm, "construction": true});
            skLineSegment(sketch, "E26.0.3.0", {"start": v(83.5, 10) * mm, "end": v(66.5, 10) * mm});
            skLineSegment(sketch, "E26.3.3.0", {"start": v(85, -8.5) * mm, "end": v(85, 8.5) * mm});
            skLineSegment(sketch, "E26.6.3.0", {"start": v(83.5, -10) * mm, "end": v(66.5, -10) * mm});
            skLineSegment(sketch, "E26.9.3.0", {"start": v(80.5, -6.56) * mm, "end": v(78.43, -4.49) * mm});
            skLineSegment(sketch, "E26.12.3.0", {"start": v(65, -8.5) * mm, "end": v(65, 8.5) * mm});
            skPoint(sketch, "E26.15.3.0", {"position": v(65, 10) * mm});
            skPoint(sketch, "E26.16.3.0", {"position": v(85, -10) * mm});
            skCircle(sketch, "E26.17.3.0", {"center": v(75, 0) * mm, "radius": 2.5 * mm});
            skLineSegment(sketch, "E26.19.3.0", {"start": v(78.1, 8.2) * mm, "end": v(80.5, 8.2) * mm});
            skPoint(sketch, "E26.22.3.0", {"position": v(71.1, -2.84) * mm});
            skPoint(sketch, "E26.23.3.0", {"position": v(78.9, 2.84) * mm});
            skLineSegment(sketch, "E26.24.3.0", {"start": v(68.44, -5.5) * mm, "end": v(70.51, -3.43) * mm});
            skLineSegment(sketch, "E26.27.3.0", {"start": v(80.5, -8.2) * mm, "end": v(78.1, -8.2) * mm});
            skPoint(sketch, "E26.30.3.0", {"position": v(65, -10) * mm});
            skLineSegment(sketch, "E26.31.3.0", {"start": v(72.99, -3.9) * mm, "end": v(77.01, -3.9) * mm});
            skLineSegment(sketch, "E26.34.3.0", {"start": v(77.01, 3.9) * mm, "end": v(72.99, 3.9) * mm});
            skLineSegment(sketch, "E26.37.3.0", {"start": v(81.56, 5.5) * mm, "end": v(79.49, 3.43) * mm});
            skPoint(sketch, "E26.40.3.0", {"position": v(65.5, 3.6) * mm});
            skPoint(sketch, "E26.41.3.0", {"position": v(84.5, -3.6) * mm});
            skLineSegment(sketch, "E26.42.3.0", {"start": v(83.2, -3.1) * mm, "end": v(83.2, -5.5) * mm});
            skLineSegment(sketch, "E26.45.3.0", {"start": v(71.57, -4.49) * mm, "end": v(69.5, -6.56) * mm});
            skPoint(sketch, "E26.48.3.0", {"position": v(65.5, -3.6) * mm});
            skPoint(sketch, "E26.49.3.0", {"position": v(84.5, 3.6) * mm});
            skLineSegment(sketch, "E26.50.3.0", {"start": v(69.5, 6.56) * mm, "end": v(71.57, 4.49) * mm});
            skLineSegment(sketch, "E26.53.3.0", {"start": v(78.9, -2.01) * mm, "end": v(78.9, 2.01) * mm});
            skLineSegment(sketch, "E26.56.3.0", {"start": v(71.1, 2.01) * mm, "end": v(71.1, -2.01) * mm});
            skLineSegment(sketch, "E26.59.3.0", {"start": v(66.8, 3.1) * mm, "end": v(66.8, 5.5) * mm});
            skPoint(sketch, "E26.62.3.0", {"position": v(85, 10) * mm});
            skPoint(sketch, "E26.63.3.0", {"position": v(78.9, -2.84) * mm});
            skPoint(sketch, "E26.64.3.0", {"position": v(71.1, 2.84) * mm});
            skPoint(sketch, "E26.65.3.0", {"position": v(75, 0) * mm});
            skPoint(sketch, "E26.66.3.0", {"position": v(78.6, -9.5) * mm});
            skPoint(sketch, "E26.67.3.0", {"position": v(72.16, 3.9) * mm});
            skPoint(sketch, "E26.68.3.0", {"position": v(71.4, 9.5) * mm});
            skLineSegment(sketch, "E26.69.3.0", {"start": v(70.51, 3.43) * mm, "end": v(68.44, 5.5) * mm});
            skPoint(sketch, "E26.72.3.0", {"position": v(77.84, -3.9) * mm});
            skPoint(sketch, "E26.73.3.0", {"position": v(78.6, 9.5) * mm});
            skLineSegment(sketch, "E26.74.3.0", {"start": v(78.43, 4.49) * mm, "end": v(80.5, 6.56) * mm});
            skLineSegment(sketch, "E26.77.3.0", {"start": v(66.8, -5.5) * mm, "end": v(66.8, -3.1) * mm});
            skPoint(sketch, "E26.80.3.0", {"position": v(77.84, 3.9) * mm});
            skLineSegment(sketch, "E26.81.3.0", {"start": v(79.49, -3.43) * mm, "end": v(81.56, -5.5) * mm});
            skLineSegment(sketch, "E26.84.3.0", {"start": v(69.5, 8.2) * mm, "end": v(71.9, 8.2) * mm});
            skLineSegment(sketch, "E26.87.3.0", {"start": v(75, 0) * mm, "end": v(75, -10) * mm, "construction": true});
            skPoint(sketch, "E26.90.3.0", {"position": v(72.16, -3.9) * mm});
            skLineSegment(sketch, "E26.91.3.0", {"start": v(83.2, 5.5) * mm, "end": v(83.2, 3.1) * mm});
            skArc(sketch, "E26.94.3.0", {"start": v(85, 8.5) * mm, "mid": v(84.56, 9.56) * mm, "end": v(83.5, 10) * mm});
            skArc(sketch, "E26.98.3.0", {"start": v(66.5, 10) * mm, "mid": v(65.44, 9.56) * mm, "end": v(65, 8.5) * mm});
            skLineSegment(sketch, "E26.102.3.0", {"start": v(71.9, -8.2) * mm, "end": v(69.5, -8.2) * mm});
            skArc(sketch, "E26.105.3.0", {"start": v(83.5, -10) * mm, "mid": v(84.56, -9.56) * mm, "end": v(85, -8.5) * mm});
            skArc(sketch, "E26.109.3.0", {"start": v(65, -8.5) * mm, "mid": v(65.44, -9.56) * mm, "end": v(66.5, -10) * mm});
            skPoint(sketch, "E26.113.3.0", {"position": v(71.4, -9.5) * mm});
            skPoint(sketch, "E26.114.3.0", {"position": v(75, 0) * mm});
            skLineSegment(sketch, "E26.115.3.0", {"start": v(78.1, -8.2) * mm, "end": v(78.1, -9.5) * mm});
            skLineSegment(sketch, "E26.118.3.0", {"start": v(66.8, -3.1) * mm, "end": v(65.5, -3.1) * mm});
            skLineSegment(sketch, "E26.121.3.0", {"start": v(68.44, -5.5) * mm, "end": v(66.8, -5.5) * mm});
            skArc(sketch, "E26.124.3.0", {"start": v(70.51, -3.43) * mm, "mid": v(70.95, -2.78) * mm, "end": v(71.1, -2.01) * mm});
            skLineSegment(sketch, "E26.128.3.0", {"start": v(71.9, 8.2) * mm, "end": v(71.9, 9.5) * mm});
            skLineSegment(sketch, "E26.131.3.0", {"start": v(83.2, 3.1) * mm, "end": v(84.5, 3.1) * mm});
            skLineSegment(sketch, "E26.134.3.0", {"start": v(81.56, 5.5) * mm, "end": v(83.2, 5.5) * mm});
            skArc(sketch, "E26.137.3.0", {"start": v(71.57, 4.49) * mm, "mid": v(72.22, 4.05) * mm, "end": v(72.99, 3.9) * mm});
            skLineSegment(sketch, "E26.141.3.0", {"start": v(69.5, 6.56) * mm, "end": v(69.5, 8.2) * mm});
            skLineSegment(sketch, "E26.144.3.0", {"start": v(84.5, -3.1) * mm, "end": v(83.2, -3.1) * mm});
            skArc(sketch, "E26.147.3.0", {"start": v(79.49, 3.43) * mm, "mid": v(79.05, 2.78) * mm, "end": v(78.9, 2.01) * mm});
            skArc(sketch, "E26.151.3.0", {"start": v(71.1, 2.01) * mm, "mid": v(70.95, 2.78) * mm, "end": v(70.51, 3.43) * mm});
            skArc(sketch, "E26.155.3.0", {"start": v(77.01, 3.9) * mm, "mid": v(77.78, 4.05) * mm, "end": v(78.43, 4.49) * mm});
            skArc(sketch, "E26.159.3.0", {"start": v(78.43, -4.49) * mm, "mid": v(77.78, -4.05) * mm, "end": v(77.01, -3.9) * mm});
            skArc(sketch, "E26.163.3.0", {"start": v(78.9, -2.01) * mm, "mid": v(79.05, -2.78) * mm, "end": v(79.49, -3.43) * mm});
            skLineSegment(sketch, "E26.167.3.0", {"start": v(68.44, 5.5) * mm, "end": v(66.8, 5.5) * mm});
            skArc(sketch, "E26.170.3.0", {"start": v(72.99, -3.9) * mm, "mid": v(72.22, -4.05) * mm, "end": v(71.57, -4.49) * mm});
            skLineSegment(sketch, "E26.174.3.0", {"start": v(80.5, 6.56) * mm, "end": v(80.5, 8.2) * mm});
            skLineSegment(sketch, "E26.177.3.0", {"start": v(69.5, -6.56) * mm, "end": v(69.5, -8.2) * mm});
            skLineSegment(sketch, "E26.180.3.0", {"start": v(81.56, -5.5) * mm, "end": v(83.2, -5.5) * mm});
            skLineSegment(sketch, "E26.183.3.0", {"start": v(80.5, -6.56) * mm, "end": v(80.5, -8.2) * mm});
            skLineSegment(sketch, "E26.186.3.0", {"start": v(65.5, 3.1) * mm, "end": v(66.8, 3.1) * mm});
            skLineSegment(sketch, "E26.189.3.0", {"start": v(78.1, 9.5) * mm, "end": v(78.1, 8.2) * mm});
            skLineSegment(sketch, "E26.192.3.0", {"start": v(71.9, -9.5) * mm, "end": v(71.9, -8.2) * mm});
            skArc(sketch, "E26.195.3.0", {"start": v(84.5, -3.4) * mm, "mid": v(84.56, -3.54) * mm, "end": v(84.7, -3.6) * mm});
            skLineSegment(sketch, "E26.199.3.0", {"start": v(85, -3.6) * mm, "end": v(84.7, -3.6) * mm});
            skLineSegment(sketch, "E26.202.3.0", {"start": v(84.5, -3.4) * mm, "end": v(84.5, -3.1) * mm});
            skArc(sketch, "E26.205.3.0", {"start": v(65.3, -3.6) * mm, "mid": v(65.44, -3.54) * mm, "end": v(65.5, -3.4) * mm});
            skArc(sketch, "E26.209.3.0", {"start": v(78.4, 9.5) * mm, "mid": v(78.54, 9.56) * mm, "end": v(78.6, 9.7) * mm});
            skLineSegment(sketch, "E26.213.3.0", {"start": v(78.1, -9.5) * mm, "end": v(78.4, -9.5) * mm});
            skArc(sketch, "E26.216.3.0", {"start": v(78.6, -9.7) * mm, "mid": v(78.54, -9.56) * mm, "end": v(78.4, -9.5) * mm});
            skLineSegment(sketch, "E26.220.3.0", {"start": v(78.6, 10) * mm, "end": v(78.6, 9.7) * mm});
            skLineSegment(sketch, "E26.223.3.0", {"start": v(65.5, -3.1) * mm, "end": v(65.5, -3.4) * mm});
            skLineSegment(sketch, "E26.226.3.0", {"start": v(78.4, 9.5) * mm, "end": v(78.1, 9.5) * mm});
            skLineSegment(sketch, "E26.229.3.0", {"start": v(65.3, -3.6) * mm, "end": v(65, -3.6) * mm});
            skLineSegment(sketch, "E26.232.3.0", {"start": v(78.6, -9.7) * mm, "end": v(78.6, -10) * mm});
            skArc(sketch, "E26.235.3.0", {"start": v(71.4, 9.7) * mm, "mid": v(71.46, 9.56) * mm, "end": v(71.6, 9.5) * mm});
            skLineSegment(sketch, "E26.239.3.0", {"start": v(71.4, -10) * mm, "end": v(71.4, -9.7) * mm});
            skLineSegment(sketch, "E26.242.3.0", {"start": v(71.6, -9.5) * mm, "end": v(71.9, -9.5) * mm});
            skLineSegment(sketch, "E26.245.3.0", {"start": v(71.4, 9.7) * mm, "end": v(71.4, 10) * mm});
            skLineSegment(sketch, "E26.248.3.0", {"start": v(71.9, 9.5) * mm, "end": v(71.6, 9.5) * mm});
            skLineSegment(sketch, "E26.251.3.0", {"start": v(65, 3.6) * mm, "end": v(65.3, 3.6) * mm});
            skArc(sketch, "E26.254.3.0", {"start": v(84.7, 3.6) * mm, "mid": v(84.56, 3.54) * mm, "end": v(84.5, 3.4) * mm});
            skArc(sketch, "E26.258.3.0", {"start": v(65.5, 3.4) * mm, "mid": v(65.44, 3.54) * mm, "end": v(65.3, 3.6) * mm});
            skLineSegment(sketch, "E26.262.3.0", {"start": v(84.7, 3.6) * mm, "end": v(85, 3.6) * mm});
            skLineSegment(sketch, "E26.265.3.0", {"start": v(65.5, 3.4) * mm, "end": v(65.5, 3.1) * mm});
            skArc(sketch, "E26.268.3.0", {"start": v(71.6, -9.5) * mm, "mid": v(71.46, -9.56) * mm, "end": v(71.4, -9.7) * mm});
            skLineSegment(sketch, "E26.272.3.0", {"start": v(84.5, 3.1) * mm, "end": v(84.5, 3.4) * mm});
            skLineSegment(sketch, "E27.0.4.0", {"start": v(108.5, 10) * mm, "end": v(91.5, 10) * mm});
            skLineSegment(sketch, "E27.3.4.0", {"start": v(110, -8.5) * mm, "end": v(110, 8.5) * mm});
            skLineSegment(sketch, "E27.6.4.0", {"start": v(108.5, -10) * mm, "end": v(91.5, -10) * mm});
            skLineSegment(sketch, "E27.9.4.0", {"start": v(105.5, -6.56) * mm, "end": v(103.43, -4.49) * mm});
            skLineSegment(sketch, "E27.12.4.0", {"start": v(90, -8.5) * mm, "end": v(90, 8.5) * mm});
            skPoint(sketch, "E27.15.4.0", {"position": v(90, 10) * mm});
            skPoint(sketch, "E27.16.4.0", {"position": v(110, -10) * mm});
            skCircle(sketch, "E27.17.4.0", {"center": v(100, 0) * mm, "radius": 2.5 * mm});
            skLineSegment(sketch, "E27.19.4.0", {"start": v(103.1, 8.2) * mm, "end": v(105.5, 8.2) * mm});
            skPoint(sketch, "E27.22.4.0", {"position": v(96.1, -2.84) * mm});
            skPoint(sketch, "E27.23.4.0", {"position": v(103.9, 2.84) * mm});
            skLineSegment(sketch, "E27.24.4.0", {"start": v(93.44, -5.5) * mm, "end": v(95.51, -3.43) * mm});
            skLineSegment(sketch, "E27.27.4.0", {"start": v(105.5, -8.2) * mm, "end": v(103.1, -8.2) * mm});
            skPoint(sketch, "E27.30.4.0", {"position": v(90, -10) * mm});
            skLineSegment(sketch, "E27.31.4.0", {"start": v(97.99, -3.9) * mm, "end": v(102.01, -3.9) * mm});
            skLineSegment(sketch, "E27.34.4.0", {"start": v(102.01, 3.9) * mm, "end": v(97.99, 3.9) * mm});
            skLineSegment(sketch, "E27.37.4.0", {"start": v(106.56, 5.5) * mm, "end": v(104.49, 3.43) * mm});
            skPoint(sketch, "E27.40.4.0", {"position": v(90.5, 3.6) * mm});
            skPoint(sketch, "E27.41.4.0", {"position": v(109.5, -3.6) * mm});
            skLineSegment(sketch, "E27.42.4.0", {"start": v(108.2, -3.1) * mm, "end": v(108.2, -5.5) * mm});
            skLineSegment(sketch, "E27.45.4.0", {"start": v(96.57, -4.49) * mm, "end": v(94.5, -6.56) * mm});
            skPoint(sketch, "E27.48.4.0", {"position": v(90.5, -3.6) * mm});
            skPoint(sketch, "E27.49.4.0", {"position": v(109.5, 3.6) * mm});
            skLineSegment(sketch, "E27.50.4.0", {"start": v(94.5, 6.56) * mm, "end": v(96.57, 4.49) * mm});
            skLineSegment(sketch, "E27.53.4.0", {"start": v(103.9, -2.01) * mm, "end": v(103.9, 2.01) * mm});
            skLineSegment(sketch, "E27.56.4.0", {"start": v(96.1, 2.01) * mm, "end": v(96.1, -2.01) * mm});
            skLineSegment(sketch, "E27.59.4.0", {"start": v(91.8, 3.1) * mm, "end": v(91.8, 5.5) * mm});
            skPoint(sketch, "E27.62.4.0", {"position": v(110, 10) * mm});
            skPoint(sketch, "E27.63.4.0", {"position": v(103.9, -2.84) * mm});
            skPoint(sketch, "E27.64.4.0", {"position": v(96.1, 2.84) * mm});
            skPoint(sketch, "E27.65.4.0", {"position": v(100, 0) * mm});
            skPoint(sketch, "E27.66.4.0", {"position": v(103.6, -9.5) * mm});
            skPoint(sketch, "E27.67.4.0", {"position": v(97.16, 3.9) * mm});
            skPoint(sketch, "E27.68.4.0", {"position": v(96.4, 9.5) * mm});
            skLineSegment(sketch, "E27.69.4.0", {"start": v(95.51, 3.43) * mm, "end": v(93.44, 5.5) * mm});
            skPoint(sketch, "E27.72.4.0", {"position": v(102.84, -3.9) * mm});
            skPoint(sketch, "E27.73.4.0", {"position": v(103.6, 9.5) * mm});
            skLineSegment(sketch, "E27.74.4.0", {"start": v(103.43, 4.49) * mm, "end": v(105.5, 6.56) * mm});
            skLineSegment(sketch, "E27.77.4.0", {"start": v(91.8, -5.5) * mm, "end": v(91.8, -3.1) * mm});
            skPoint(sketch, "E27.80.4.0", {"position": v(102.84, 3.9) * mm});
            skLineSegment(sketch, "E27.81.4.0", {"start": v(104.49, -3.43) * mm, "end": v(106.56, -5.5) * mm});
            skLineSegment(sketch, "E27.84.4.0", {"start": v(94.5, 8.2) * mm, "end": v(96.9, 8.2) * mm});
            skLineSegment(sketch, "E27.87.4.0", {"start": v(100, 0) * mm, "end": v(100, -10) * mm, "construction": true});
            skPoint(sketch, "E27.90.4.0", {"position": v(97.16, -3.9) * mm});
            skLineSegment(sketch, "E27.91.4.0", {"start": v(108.2, 5.5) * mm, "end": v(108.2, 3.1) * mm});
            skArc(sketch, "E27.94.4.0", {"start": v(110, 8.5) * mm, "mid": v(109.56, 9.56) * mm, "end": v(108.5, 10) * mm});
            skArc(sketch, "E27.98.4.0", {"start": v(91.5, 10) * mm, "mid": v(90.44, 9.56) * mm, "end": v(90, 8.5) * mm});
            skLineSegment(sketch, "E27.102.4.0", {"start": v(96.9, -8.2) * mm, "end": v(94.5, -8.2) * mm});
            skArc(sketch, "E27.105.4.0", {"start": v(108.5, -10) * mm, "mid": v(109.56, -9.56) * mm, "end": v(110, -8.5) * mm});
            skArc(sketch, "E27.109.4.0", {"start": v(90, -8.5) * mm, "mid": v(90.44, -9.56) * mm, "end": v(91.5, -10) * mm});
            skPoint(sketch, "E27.113.4.0", {"position": v(96.4, -9.5) * mm});
            skPoint(sketch, "E27.114.4.0", {"position": v(100, 0) * mm});
            skLineSegment(sketch, "E27.115.4.0", {"start": v(103.1, -8.2) * mm, "end": v(103.1, -9.5) * mm});
            skLineSegment(sketch, "E27.118.4.0", {"start": v(91.8, -3.1) * mm, "end": v(90.5, -3.1) * mm});
            skLineSegment(sketch, "E27.121.4.0", {"start": v(93.44, -5.5) * mm, "end": v(91.8, -5.5) * mm});
            skArc(sketch, "E27.124.4.0", {"start": v(95.51, -3.43) * mm, "mid": v(95.95, -2.78) * mm, "end": v(96.1, -2.01) * mm});
            skLineSegment(sketch, "E27.128.4.0", {"start": v(96.9, 8.2) * mm, "end": v(96.9, 9.5) * mm});
            skLineSegment(sketch, "E27.131.4.0", {"start": v(108.2, 3.1) * mm, "end": v(109.5, 3.1) * mm});
            skLineSegment(sketch, "E27.134.4.0", {"start": v(106.56, 5.5) * mm, "end": v(108.2, 5.5) * mm});
            skArc(sketch, "E27.137.4.0", {"start": v(96.57, 4.49) * mm, "mid": v(97.22, 4.05) * mm, "end": v(97.99, 3.9) * mm});
            skLineSegment(sketch, "E27.141.4.0", {"start": v(94.5, 6.56) * mm, "end": v(94.5, 8.2) * mm});
            skLineSegment(sketch, "E27.144.4.0", {"start": v(109.5, -3.1) * mm, "end": v(108.2, -3.1) * mm});
            skArc(sketch, "E27.147.4.0", {"start": v(104.49, 3.43) * mm, "mid": v(104.05, 2.78) * mm, "end": v(103.9, 2.01) * mm});
            skArc(sketch, "E27.151.4.0", {"start": v(96.1, 2.01) * mm, "mid": v(95.95, 2.78) * mm, "end": v(95.51, 3.43) * mm});
            skArc(sketch, "E27.155.4.0", {"start": v(102.01, 3.9) * mm, "mid": v(102.78, 4.05) * mm, "end": v(103.43, 4.49) * mm});
            skArc(sketch, "E27.159.4.0", {"start": v(103.43, -4.49) * mm, "mid": v(102.78, -4.05) * mm, "end": v(102.01, -3.9) * mm});
            skArc(sketch, "E27.163.4.0", {"start": v(103.9, -2.01) * mm, "mid": v(104.05, -2.78) * mm, "end": v(104.49, -3.43) * mm});
            skLineSegment(sketch, "E27.167.4.0", {"start": v(93.44, 5.5) * mm, "end": v(91.8, 5.5) * mm});
            skArc(sketch, "E27.170.4.0", {"start": v(97.99, -3.9) * mm, "mid": v(97.22, -4.05) * mm, "end": v(96.57, -4.49) * mm});
            skLineSegment(sketch, "E27.174.4.0", {"start": v(105.5, 6.56) * mm, "end": v(105.5, 8.2) * mm});
            skLineSegment(sketch, "E27.177.4.0", {"start": v(94.5, -6.56) * mm, "end": v(94.5, -8.2) * mm});
            skLineSegment(sketch, "E27.180.4.0", {"start": v(106.56, -5.5) * mm, "end": v(108.2, -5.5) * mm});
            skLineSegment(sketch, "E27.183.4.0", {"start": v(105.5, -6.56) * mm, "end": v(105.5, -8.2) * mm});
            skLineSegment(sketch, "E27.186.4.0", {"start": v(90.5, 3.1) * mm, "end": v(91.8, 3.1) * mm});
            skLineSegment(sketch, "E27.189.4.0", {"start": v(103.1, 9.5) * mm, "end": v(103.1, 8.2) * mm});
            skLineSegment(sketch, "E27.192.4.0", {"start": v(96.9, -9.5) * mm, "end": v(96.9, -8.2) * mm});
            skArc(sketch, "E27.195.4.0", {"start": v(109.5, -3.4) * mm, "mid": v(109.56, -3.54) * mm, "end": v(109.7, -3.6) * mm});
            skLineSegment(sketch, "E27.199.4.0", {"start": v(110, -3.6) * mm, "end": v(109.7, -3.6) * mm});
            skLineSegment(sketch, "E27.202.4.0", {"start": v(109.5, -3.4) * mm, "end": v(109.5, -3.1) * mm});
            skArc(sketch, "E27.205.4.0", {"start": v(90.3, -3.6) * mm, "mid": v(90.44, -3.54) * mm, "end": v(90.5, -3.4) * mm});
            skArc(sketch, "E27.209.4.0", {"start": v(103.4, 9.5) * mm, "mid": v(103.54, 9.56) * mm, "end": v(103.6, 9.7) * mm});
            skLineSegment(sketch, "E27.213.4.0", {"start": v(103.1, -9.5) * mm, "end": v(103.4, -9.5) * mm});
            skArc(sketch, "E27.216.4.0", {"start": v(103.6, -9.7) * mm, "mid": v(103.54, -9.56) * mm, "end": v(103.4, -9.5) * mm});
            skLineSegment(sketch, "E27.220.4.0", {"start": v(103.6, 10) * mm, "end": v(103.6, 9.7) * mm});
            skLineSegment(sketch, "E27.223.4.0", {"start": v(90.5, -3.1) * mm, "end": v(90.5, -3.4) * mm});
            skLineSegment(sketch, "E27.226.4.0", {"start": v(103.4, 9.5) * mm, "end": v(103.1, 9.5) * mm});
            skLineSegment(sketch, "E27.229.4.0", {"start": v(90.3, -3.6) * mm, "end": v(90, -3.6) * mm});
            skLineSegment(sketch, "E27.232.4.0", {"start": v(103.6, -9.7) * mm, "end": v(103.6, -10) * mm});
            skArc(sketch, "E27.235.4.0", {"start": v(96.4, 9.7) * mm, "mid": v(96.46, 9.56) * mm, "end": v(96.6, 9.5) * mm});
            skLineSegment(sketch, "E27.239.4.0", {"start": v(96.4, -10) * mm, "end": v(96.4, -9.7) * mm});
            skLineSegment(sketch, "E27.242.4.0", {"start": v(96.6, -9.5) * mm, "end": v(96.9, -9.5) * mm});
            skLineSegment(sketch, "E27.245.4.0", {"start": v(96.4, 9.7) * mm, "end": v(96.4, 10) * mm});
            skLineSegment(sketch, "E27.248.4.0", {"start": v(96.9, 9.5) * mm, "end": v(96.6, 9.5) * mm});
            skLineSegment(sketch, "E27.251.4.0", {"start": v(90, 3.6) * mm, "end": v(90.3, 3.6) * mm});
            skArc(sketch, "E27.254.4.0", {"start": v(109.7, 3.6) * mm, "mid": v(109.56, 3.54) * mm, "end": v(109.5, 3.4) * mm});
            skArc(sketch, "E27.258.4.0", {"start": v(90.5, 3.4) * mm, "mid": v(90.44, 3.54) * mm, "end": v(90.3, 3.6) * mm});
            skLineSegment(sketch, "E27.262.4.0", {"start": v(109.7, 3.6) * mm, "end": v(110, 3.6) * mm});
            skLineSegment(sketch, "E27.265.4.0", {"start": v(90.5, 3.4) * mm, "end": v(90.5, 3.1) * mm});
            skArc(sketch, "E27.268.4.0", {"start": v(96.6, -9.5) * mm, "mid": v(96.46, -9.56) * mm, "end": v(96.4, -9.7) * mm});
            skLineSegment(sketch, "E27.272.4.0", {"start": v(109.5, 3.1) * mm, "end": v(109.5, 3.4) * mm});
            skLineSegment(sketch, "E27.0.5.0", {"start": v(133.5, 10) * mm, "end": v(116.5, 10) * mm});
            skLineSegment(sketch, "E27.3.5.0", {"start": v(135, -8.5) * mm, "end": v(135, 8.5) * mm});
            skLineSegment(sketch, "E27.6.5.0", {"start": v(133.5, -10) * mm, "end": v(116.5, -10) * mm});
            skLineSegment(sketch, "E27.9.5.0", {"start": v(130.5, -6.56) * mm, "end": v(128.43, -4.49) * mm});
            skLineSegment(sketch, "E27.12.5.0", {"start": v(115, -8.5) * mm, "end": v(115, 8.5) * mm});
            skPoint(sketch, "E27.15.5.0", {"position": v(115, 10) * mm});
            skPoint(sketch, "E27.16.5.0", {"position": v(135, -10) * mm});
            skCircle(sketch, "E27.17.5.0", {"center": v(125, 0) * mm, "radius": 2.5 * mm});
            skLineSegment(sketch, "E27.19.5.0", {"start": v(128.1, 8.2) * mm, "end": v(130.5, 8.2) * mm});
            skPoint(sketch, "E27.22.5.0", {"position": v(121.1, -2.84) * mm});
            skPoint(sketch, "E27.23.5.0", {"position": v(128.9, 2.84) * mm});
            skLineSegment(sketch, "E27.24.5.0", {"start": v(118.44, -5.5) * mm, "end": v(120.51, -3.43) * mm});
            skLineSegment(sketch, "E27.27.5.0", {"start": v(130.5, -8.2) * mm, "end": v(128.1, -8.2) * mm});
            skPoint(sketch, "E27.30.5.0", {"position": v(115, -10) * mm});
            skLineSegment(sketch, "E27.31.5.0", {"start": v(122.99, -3.9) * mm, "end": v(127.01, -3.9) * mm});
            skLineSegment(sketch, "E27.34.5.0", {"start": v(127.01, 3.9) * mm, "end": v(122.99, 3.9) * mm});
            skLineSegment(sketch, "E27.37.5.0", {"start": v(131.56, 5.5) * mm, "end": v(129.49, 3.43) * mm});
            skPoint(sketch, "E27.40.5.0", {"position": v(115.5, 3.6) * mm});
            skPoint(sketch, "E27.41.5.0", {"position": v(134.5, -3.6) * mm});
            skLineSegment(sketch, "E27.42.5.0", {"start": v(133.2, -3.1) * mm, "end": v(133.2, -5.5) * mm});
            skLineSegment(sketch, "E27.45.5.0", {"start": v(121.57, -4.49) * mm, "end": v(119.5, -6.56) * mm});
            skPoint(sketch, "E27.48.5.0", {"position": v(115.5, -3.6) * mm});
            skPoint(sketch, "E27.49.5.0", {"position": v(134.5, 3.6) * mm});
            skLineSegment(sketch, "E27.50.5.0", {"start": v(119.5, 6.56) * mm, "end": v(121.57, 4.49) * mm});
            skLineSegment(sketch, "E27.53.5.0", {"start": v(128.9, -2.01) * mm, "end": v(128.9, 2.01) * mm});
            skLineSegment(sketch, "E27.56.5.0", {"start": v(121.1, 2.01) * mm, "end": v(121.1, -2.01) * mm});
            skLineSegment(sketch, "E27.59.5.0", {"start": v(116.8, 3.1) * mm, "end": v(116.8, 5.5) * mm});
            skPoint(sketch, "E27.62.5.0", {"position": v(135, 10) * mm});
            skPoint(sketch, "E27.63.5.0", {"position": v(128.9, -2.84) * mm});
            skPoint(sketch, "E27.64.5.0", {"position": v(121.1, 2.84) * mm});
            skPoint(sketch, "E27.65.5.0", {"position": v(125, 0) * mm});
            skPoint(sketch, "E27.66.5.0", {"position": v(128.6, -9.5) * mm});
            skPoint(sketch, "E27.67.5.0", {"position": v(122.16, 3.9) * mm});
            skPoint(sketch, "E27.68.5.0", {"position": v(121.4, 9.5) * mm});
            skLineSegment(sketch, "E27.69.5.0", {"start": v(120.51, 3.43) * mm, "end": v(118.44, 5.5) * mm});
            skPoint(sketch, "E27.72.5.0", {"position": v(127.84, -3.9) * mm});
            skPoint(sketch, "E27.73.5.0", {"position": v(128.6, 9.5) * mm});
            skLineSegment(sketch, "E27.74.5.0", {"start": v(128.43, 4.49) * mm, "end": v(130.5, 6.56) * mm});
            skLineSegment(sketch, "E27.77.5.0", {"start": v(116.8, -5.5) * mm, "end": v(116.8, -3.1) * mm});
            skPoint(sketch, "E27.80.5.0", {"position": v(127.84, 3.9) * mm});
            skLineSegment(sketch, "E27.81.5.0", {"start": v(129.49, -3.43) * mm, "end": v(131.56, -5.5) * mm});
            skLineSegment(sketch, "E27.84.5.0", {"start": v(119.5, 8.2) * mm, "end": v(121.9, 8.2) * mm});
            skLineSegment(sketch, "E27.87.5.0", {"start": v(125, 0) * mm, "end": v(125, -10) * mm, "construction": true});
            skPoint(sketch, "E27.90.5.0", {"position": v(122.16, -3.9) * mm});
            skLineSegment(sketch, "E27.91.5.0", {"start": v(133.2, 5.5) * mm, "end": v(133.2, 3.1) * mm});
            skArc(sketch, "E27.94.5.0", {"start": v(135, 8.5) * mm, "mid": v(134.56, 9.56) * mm, "end": v(133.5, 10) * mm});
            skArc(sketch, "E27.98.5.0", {"start": v(116.5, 10) * mm, "mid": v(115.44, 9.56) * mm, "end": v(115, 8.5) * mm});
            skLineSegment(sketch, "E27.102.5.0", {"start": v(121.9, -8.2) * mm, "end": v(119.5, -8.2) * mm});
            skArc(sketch, "E27.105.5.0", {"start": v(133.5, -10) * mm, "mid": v(134.56, -9.56) * mm, "end": v(135, -8.5) * mm});
            skArc(sketch, "E27.109.5.0", {"start": v(115, -8.5) * mm, "mid": v(115.44, -9.56) * mm, "end": v(116.5, -10) * mm});
            skPoint(sketch, "E27.113.5.0", {"position": v(121.4, -9.5) * mm});
            skPoint(sketch, "E27.114.5.0", {"position": v(125, 0) * mm});
            skLineSegment(sketch, "E27.115.5.0", {"start": v(128.1, -8.2) * mm, "end": v(128.1, -9.5) * mm});
            skLineSegment(sketch, "E27.118.5.0", {"start": v(116.8, -3.1) * mm, "end": v(115.5, -3.1) * mm});
            skLineSegment(sketch, "E27.121.5.0", {"start": v(118.44, -5.5) * mm, "end": v(116.8, -5.5) * mm});
            skArc(sketch, "E27.124.5.0", {"start": v(120.51, -3.43) * mm, "mid": v(120.95, -2.78) * mm, "end": v(121.1, -2.01) * mm});
            skLineSegment(sketch, "E27.128.5.0", {"start": v(121.9, 8.2) * mm, "end": v(121.9, 9.5) * mm});
            skLineSegment(sketch, "E27.131.5.0", {"start": v(133.2, 3.1) * mm, "end": v(134.5, 3.1) * mm});
            skLineSegment(sketch, "E27.134.5.0", {"start": v(131.56, 5.5) * mm, "end": v(133.2, 5.5) * mm});
            skArc(sketch, "E27.137.5.0", {"start": v(121.57, 4.49) * mm, "mid": v(122.22, 4.05) * mm, "end": v(122.99, 3.9) * mm});
            skLineSegment(sketch, "E27.141.5.0", {"start": v(119.5, 6.56) * mm, "end": v(119.5, 8.2) * mm});
            skLineSegment(sketch, "E27.144.5.0", {"start": v(134.5, -3.1) * mm, "end": v(133.2, -3.1) * mm});
            skArc(sketch, "E27.147.5.0", {"start": v(129.49, 3.43) * mm, "mid": v(129.05, 2.78) * mm, "end": v(128.9, 2.01) * mm});
            skArc(sketch, "E27.151.5.0", {"start": v(121.1, 2.01) * mm, "mid": v(120.95, 2.78) * mm, "end": v(120.51, 3.43) * mm});
            skArc(sketch, "E27.155.5.0", {"start": v(127.01, 3.9) * mm, "mid": v(127.78, 4.05) * mm, "end": v(128.43, 4.49) * mm});
            skArc(sketch, "E27.159.5.0", {"start": v(128.43, -4.49) * mm, "mid": v(127.78, -4.05) * mm, "end": v(127.01, -3.9) * mm});
            skArc(sketch, "E27.163.5.0", {"start": v(128.9, -2.01) * mm, "mid": v(129.05, -2.78) * mm, "end": v(129.49, -3.43) * mm});
            skLineSegment(sketch, "E27.167.5.0", {"start": v(118.44, 5.5) * mm, "end": v(116.8, 5.5) * mm});
            skArc(sketch, "E27.170.5.0", {"start": v(122.99, -3.9) * mm, "mid": v(122.22, -4.05) * mm, "end": v(121.57, -4.49) * mm});
            skLineSegment(sketch, "E27.174.5.0", {"start": v(130.5, 6.56) * mm, "end": v(130.5, 8.2) * mm});
            skLineSegment(sketch, "E27.177.5.0", {"start": v(119.5, -6.56) * mm, "end": v(119.5, -8.2) * mm});
            skLineSegment(sketch, "E27.180.5.0", {"start": v(131.56, -5.5) * mm, "end": v(133.2, -5.5) * mm});
            skLineSegment(sketch, "E27.183.5.0", {"start": v(130.5, -6.56) * mm, "end": v(130.5, -8.2) * mm});
            skLineSegment(sketch, "E27.186.5.0", {"start": v(115.5, 3.1) * mm, "end": v(116.8, 3.1) * mm});
            skLineSegment(sketch, "E27.189.5.0", {"start": v(128.1, 9.5) * mm, "end": v(128.1, 8.2) * mm});
            skLineSegment(sketch, "E27.192.5.0", {"start": v(121.9, -9.5) * mm, "end": v(121.9, -8.2) * mm});
            skArc(sketch, "E27.195.5.0", {"start": v(134.5, -3.4) * mm, "mid": v(134.56, -3.54) * mm, "end": v(134.7, -3.6) * mm});
            skLineSegment(sketch, "E27.199.5.0", {"start": v(135, -3.6) * mm, "end": v(134.7, -3.6) * mm});
            skLineSegment(sketch, "E27.202.5.0", {"start": v(134.5, -3.4) * mm, "end": v(134.5, -3.1) * mm});
            skArc(sketch, "E27.205.5.0", {"start": v(115.3, -3.6) * mm, "mid": v(115.44, -3.54) * mm, "end": v(115.5, -3.4) * mm});
            skArc(sketch, "E27.209.5.0", {"start": v(128.4, 9.5) * mm, "mid": v(128.54, 9.56) * mm, "end": v(128.6, 9.7) * mm});
            skLineSegment(sketch, "E27.213.5.0", {"start": v(128.1, -9.5) * mm, "end": v(128.4, -9.5) * mm});
            skArc(sketch, "E27.216.5.0", {"start": v(128.6, -9.7) * mm, "mid": v(128.54, -9.56) * mm, "end": v(128.4, -9.5) * mm});
            skLineSegment(sketch, "E27.220.5.0", {"start": v(128.6, 10) * mm, "end": v(128.6, 9.7) * mm});
            skLineSegment(sketch, "E27.223.5.0", {"start": v(115.5, -3.1) * mm, "end": v(115.5, -3.4) * mm});
            skLineSegment(sketch, "E27.226.5.0", {"start": v(128.4, 9.5) * mm, "end": v(128.1, 9.5) * mm});
            skLineSegment(sketch, "E27.229.5.0", {"start": v(115.3, -3.6) * mm, "end": v(115, -3.6) * mm});
            skLineSegment(sketch, "E27.232.5.0", {"start": v(128.6, -9.7) * mm, "end": v(128.6, -10) * mm});
            skArc(sketch, "E27.235.5.0", {"start": v(121.4, 9.7) * mm, "mid": v(121.46, 9.56) * mm, "end": v(121.6, 9.5) * mm});
            skLineSegment(sketch, "E27.239.5.0", {"start": v(121.4, -10) * mm, "end": v(121.4, -9.7) * mm});
            skLineSegment(sketch, "E27.242.5.0", {"start": v(121.6, -9.5) * mm, "end": v(121.9, -9.5) * mm});
            skLineSegment(sketch, "E27.245.5.0", {"start": v(121.4, 9.7) * mm, "end": v(121.4, 10) * mm});
            skLineSegment(sketch, "E27.248.5.0", {"start": v(121.9, 9.5) * mm, "end": v(121.6, 9.5) * mm});
            skLineSegment(sketch, "E27.251.5.0", {"start": v(115, 3.6) * mm, "end": v(115.3, 3.6) * mm});
            skArc(sketch, "E27.254.5.0", {"start": v(134.7, 3.6) * mm, "mid": v(134.56, 3.54) * mm, "end": v(134.5, 3.4) * mm});
            skArc(sketch, "E27.258.5.0", {"start": v(115.5, 3.4) * mm, "mid": v(115.44, 3.54) * mm, "end": v(115.3, 3.6) * mm});
            skLineSegment(sketch, "E27.262.5.0", {"start": v(134.7, 3.6) * mm, "end": v(135, 3.6) * mm});
            skLineSegment(sketch, "E27.265.5.0", {"start": v(115.5, 3.4) * mm, "end": v(115.5, 3.1) * mm});
            skArc(sketch, "E27.268.5.0", {"start": v(121.6, -9.5) * mm, "mid": v(121.46, -9.56) * mm, "end": v(121.4, -9.7) * mm});
            skLineSegment(sketch, "E27.272.5.0", {"start": v(134.5, 3.1) * mm, "end": v(134.5, 3.4) * mm});
            skLineSegment(sketch, "E28.bottom", {"start": v(10, 15) * mm, "end": v(-10, 15) * mm});
            skLineSegment(sketch, "E28.top", {"start": v(10, 35) * mm, "end": v(-10, 35) * mm});
            skLineSegment(sketch, "E28.left", {"start": v(10, 15) * mm, "end": v(10, 35) * mm});
            skLineSegment(sketch, "E28.right", {"start": v(-10, 15) * mm, "end": v(-10, 35) * mm});
            skPoint(sketch, "E28.middle", {"position": v(0, 25) * mm});
            skLineSegment(sketch, "E29.1.0.0", {"start": v(35, 35) * mm, "end": v(15, 35) * mm});
            skLineSegment(sketch, "E29.1.0.1", {"start": v(35, 15) * mm, "end": v(15, 15) * mm});
            skPoint(sketch, "E29.1.0.2", {"position": v(25, 25) * mm});
            skLineSegment(sketch, "E29.1.0.3", {"start": v(15, 15) * mm, "end": v(15, 35) * mm});
            skLineSegment(sketch, "E29.1.0.4", {"start": v(35, 15) * mm, "end": v(35, 35) * mm});
            skLineSegment(sketch, "E29.2.0.0", {"start": v(60, 35) * mm, "end": v(40, 35) * mm});
            skLineSegment(sketch, "E29.2.0.1", {"start": v(60, 15) * mm, "end": v(40, 15) * mm});
            skPoint(sketch, "E29.2.0.2", {"position": v(50, 25) * mm});
            skLineSegment(sketch, "E29.2.0.3", {"start": v(40, 15) * mm, "end": v(40, 35) * mm});
            skLineSegment(sketch, "E29.2.0.4", {"start": v(60, 15) * mm, "end": v(60, 35) * mm});
            skLineSegment(sketch, "E29.direction1", {"start": v(-10, 15) * mm, "end": v(15, 15) * mm, "construction": true});
            skLineSegment(sketch, "E30.0.3.0", {"start": v(85, 35) * mm, "end": v(65, 35) * mm});
            skLineSegment(sketch, "E30.3.3.0", {"start": v(85, 15) * mm, "end": v(65, 15) * mm});
            skPoint(sketch, "E30.6.3.0", {"position": v(75, 25) * mm});
            skLineSegment(sketch, "E30.7.3.0", {"start": v(65, 15) * mm, "end": v(65, 35) * mm});
            skLineSegment(sketch, "E30.10.3.0", {"start": v(85, 15) * mm, "end": v(85, 35) * mm});
            skLineSegment(sketch, "E30.0.4.0", {"start": v(110, 35) * mm, "end": v(90, 35) * mm});
            skLineSegment(sketch, "E30.3.4.0", {"start": v(110, 15) * mm, "end": v(90, 15) * mm});
            skPoint(sketch, "E30.6.4.0", {"position": v(100, 25) * mm});
            skLineSegment(sketch, "E30.7.4.0", {"start": v(90, 15) * mm, "end": v(90, 35) * mm});
            skLineSegment(sketch, "E30.10.4.0", {"start": v(110, 15) * mm, "end": v(110, 35) * mm});
            skLineSegment(sketch, "E30.0.5.0", {"start": v(135, 35) * mm, "end": v(115, 35) * mm});
            skLineSegment(sketch, "E30.3.5.0", {"start": v(135, 15) * mm, "end": v(115, 15) * mm});
            skPoint(sketch, "E30.6.5.0", {"position": v(125, 25) * mm});
            skLineSegment(sketch, "E30.7.5.0", {"start": v(115, 15) * mm, "end": v(115, 35) * mm});
            skLineSegment(sketch, "E30.10.5.0", {"start": v(135, 15) * mm, "end": v(135, 35) * mm});
            skSolve(sketch);
        }
        {
            var Q0;
            Q0=makeQuery(id+"F3.imprint","IMPRINT",FACE,{"disambiguationData":[TD([[makeQuery(id+"F3.imprint","IMPRINT",EDGE,{"derivedFrom":sQuery(id+"F3.wireOp",EDGE,"E28.bottom")}),-1.0]])]});
            extrude(context, id + "F4", {"entities" : qUnion([Q0]), "depth" : (getVariable(context, 'X')) * mm, "offsetDistance" : 25 * mm});
        }
        {
            var Q0;
            Q0=makeQuery(id+"F3.imprint","IMPRINT",FACE,{"disambiguationData":[TD([[makeQuery(id+"F3.imprint","IMPRINT",EDGE,{"derivedFrom":sQuery(id+"F3.wireOp",EDGE,"E29.1.0.0")}),1.0]])]});
            extrude(context, id + "F5", {"entities" : qUnion([Q0]), "depth" : (getVariable(context, 'Y')) * mm, "offsetDistance" : 25 * mm});
        }
        {
            var Q0;
            Q0=makeQuery(id+"F3.imprint","IMPRINT",FACE,{"disambiguationData":[TD([[makeQuery(id+"F3.imprint","IMPRINT",EDGE,{"derivedFrom":sQuery(id+"F3.wireOp",EDGE,"E29.2.0.0")}),1.0]])]});
            extrude(context, id + "F6", {"entities" : qUnion([Q0]), "depth" : (getVariable(context, 'Y') + 20 * 2) * mm, "offsetDistance" : 25 * mm});
        }
        {
            var Q0;
            Q0=makeQuery(id+"F3.imprint","IMPRINT",FACE,{"disambiguationData":[TD([[makeQuery(id+"F3.imprint","IMPRINT",EDGE,{"derivedFrom":sQuery(id+"F3.wireOp",EDGE,"E30.0.3.0")}),1.0]])]});
            extrude(context, id + "F7", {"entities" : qUnion([Q0]), "depth" : getVariable(context, 'Z') * mm, "offsetDistance" : 25 * mm});
        }
        {
            var Q0;
            Q0=qCreatedBy(makeId("Top.planeOp"),FACE);
            var sketch = newSketch(context, id + "F8", { "sketchPlane" : qUnion([Q0])});
            skCircle(sketch, "E31", {"center": v(0, -50) * mm, "radius": 4 * mm});
            skCircle(sketch, "E32.1.0.0", {"center": v(25, -50) * mm, "radius": 4 * mm});
            skCircle(sketch, "E32.2.0.0", {"center": v(50, -50) * mm, "radius": 4 * mm});
            skLineSegment(sketch, "E32.direction1", {"start": v(0, -50) * mm, "end": v(25, -50) * mm, "construction": true});
            skSolve(sketch);
        }
        {
            var Q0;
            Q0=makeQuery(id+"F8.imprint","IMPRINT",FACE,{"disambiguationData":[TD([[makeQuery(id+"F8.imprint","IMPRINT",EDGE,{"derivedFrom":sQuery(id+"F8.wireOp",EDGE,"E31")}),1.0]])]});
            extrude(context, id + "F9", {"entities" : qUnion([Q0]), "depth" : 400 * mm, "offsetDistance" : 25 * mm});
        }
        {
            var Q0;
            Q0=makeQuery(id+"F8.imprint","IMPRINT",FACE,{"disambiguationData":[TD([[makeQuery(id+"F8.imprint","IMPRINT",EDGE,{"derivedFrom":sQuery(id+"F8.wireOp",EDGE,"E32.1.0.0")}),1.0]])]});
            extrude(context, id + "F10", {"entities" : qUnion([Q0]), "depth" : 300 * mm, "offsetDistance" : 25 * mm});
        }
        {
            var Q0;
            Q0=makeQuery(id+"F8.imprint","IMPRINT",FACE,{"disambiguationData":[TD([[makeQuery(id+"F8.imprint","IMPRINT",EDGE,{"derivedFrom":sQuery(id+"F8.wireOp",EDGE,"E32.2.0.0")}),1.0]])]});
            extrude(context, id + "F11", {"entities" : qUnion([Q0]), "depth" : 400 * mm, "offsetDistance" : 25 * mm});
        }
        {
            var Q0;
            Q0=qCreatedBy(makeId("Top.planeOp"),FACE);
            var sketch = newSketch(context, id + "F12", { "sketchPlane" : qUnion([Q0])});
            skCircle(sketch, "E33", {"center": v(0, -100) * mm, "radius": 8 * mm});
            skCircle(sketch, "E34", {"center": v(0, -100) * mm, "radius": 2.5 * mm});
            skLineSegment(sketch, "E35.bottom", {"start": v(63, -115) * mm, "end": v(37, -115) * mm});
            skLineSegment(sketch, "E35.top", {"start": v(63, -85) * mm, "end": v(37, -85) * mm});
            skLineSegment(sketch, "E35.left", {"start": v(65, -113) * mm, "end": v(65, -87) * mm});
            skLineSegment(sketch, "E35.right", {"start": v(35, -113) * mm, "end": v(35, -87) * mm});
            skPoint(sketch, "E35.middle", {"position": v(50, -100) * mm});
            skPoint(sketch, "E36.visualSharp", {"position": v(35, -85) * mm});
            skArc(sketch, "E36.filletArc", {"start": v(37, -85) * mm, "mid": v(35.59, -85.59) * mm, "end": v(35, -87) * mm});
            skPoint(sketch, "E37.visualSharp", {"position": v(65, -85) * mm});
            skArc(sketch, "E37.filletArc", {"start": v(65, -87) * mm, "mid": v(64.41, -85.59) * mm, "end": v(63, -85) * mm});
            skPoint(sketch, "E38.visualSharp", {"position": v(65, -115) * mm});
            skArc(sketch, "E38.filletArc", {"start": v(63, -115) * mm, "mid": v(64.41, -114.41) * mm, "end": v(65, -113) * mm});
            skPoint(sketch, "E39.visualSharp", {"position": v(35, -115) * mm});
            skArc(sketch, "E39.filletArc", {"start": v(35, -113) * mm, "mid": v(35.59, -114.41) * mm, "end": v(37, -115) * mm});
            skLineSegment(sketch, "E40.bottom", {"start": v(62, -112) * mm, "end": v(38, -112) * mm, "construction": true});
            skLineSegment(sketch, "E40.top", {"start": v(62, -88) * mm, "end": v(38, -88) * mm, "construction": true});
            skLineSegment(sketch, "E40.left", {"start": v(62, -112) * mm, "end": v(62, -88) * mm, "construction": true});
            skLineSegment(sketch, "E40.right", {"start": v(38, -112) * mm, "end": v(38, -88) * mm, "construction": true});
            skCircle(sketch, "E41", {"center": v(38, -88) * mm, "radius": 1.5 * mm});
            skCircle(sketch, "E42", {"center": v(62, -88) * mm, "radius": 1.5 * mm});
            skCircle(sketch, "E43", {"center": v(38, -112) * mm, "radius": 1.5 * mm});
            skCircle(sketch, "E44", {"center": v(62, -112) * mm, "radius": 1.5 * mm});
            skCircle(sketch, "E45", {"center": v(50, -100) * mm, "radius": 14.25 * mm});
            skCircle(sketch, "E46", {"center": v(50, -100) * mm, "radius": 7.5 * mm});
            skLineSegment(sketch, "E47", {"start": v(57.5, -100) * mm, "end": v(64.25, -100) * mm});
            skLineSegment(sketch, "E48", {"start": v(57.24, -101.94) * mm, "end": v(63.76, -103.69) * mm});
            skLineSegment(sketch, "E49.1.0", {"start": v(54.68, -94.14) * mm, "end": v(58.88, -88.86) * mm});
            skLineSegment(sketch, "E49.1.1", {"start": v(56.03, -95.55) * mm, "end": v(61.47, -91.54) * mm});
            skLineSegment(sketch, "E49.2.0", {"start": v(48.33, -92.69) * mm, "end": v(46.83, -86.1) * mm});
            skLineSegment(sketch, "E49.2.1", {"start": v(50.28, -92.5) * mm, "end": v(50.53, -85.76) * mm});
            skLineSegment(sketch, "E50.1.3.0", {"start": v(43.24, -96.75) * mm, "end": v(37.16, -93.82) * mm});
            skLineSegment(sketch, "E50.3.3.0", {"start": v(44.32, -95.1) * mm, "end": v(39.2, -90.7) * mm});
            skLineSegment(sketch, "E50.1.4.0", {"start": v(43.24, -103.25) * mm, "end": v(37.16, -106.18) * mm});
            skLineSegment(sketch, "E50.3.4.0", {"start": v(42.63, -101.4) * mm, "end": v(36, -102.65) * mm});
            skLineSegment(sketch, "E51.1.5.0", {"start": v(48.33, -107.31) * mm, "end": v(46.83, -113.9) * mm});
            skLineSegment(sketch, "E51.3.5.0", {"start": v(46.5, -106.63) * mm, "end": v(43.34, -112.6) * mm});
            skLineSegment(sketch, "E51.1.6.0", {"start": v(54.68, -105.86) * mm, "end": v(58.88, -111.14) * mm});
            skLineSegment(sketch, "E51.3.6.0", {"start": v(53, -106.87) * mm, "end": v(55.7, -113.06) * mm});
            skCircle(sketch, "E52", {"center": v(-50, -100) * mm, "radius": 7.5 * mm});
            skCircle(sketch, "E53", {"center": v(-50, -100) * mm, "radius": 4 * mm});
            skCircle(sketch, "E54", {"center": v(-50, -100) * mm, "radius": 7.15 * mm});
            skSolve(sketch);
        }
        {
            var Q0;
            Q0=makeQuery(id+"F12.imprint","IMPRINT",FACE,{"disambiguationData":[TD([[makeQuery(id+"F12.imprint","IMPRINT",EDGE,{"derivedFrom":sQuery(id+"F12.wireOp",EDGE,"E33")}),1.0]])]});
            extrude(context, id + "F13", {"entities" : qUnion([Q0]), "depth" : 5 * mm, "offsetDistance" : 25 * mm});
        }
        {
            var Q0;
            Q0=makeQuery(id+"F12.imprint","IMPRINT",FACE,{"disambiguationData":[TD([[makeQuery(id+"F12.imprint","IMPRINT",EDGE,{"derivedFrom":sQuery(id+"F12.wireOp",EDGE,"E35.bottom")}),-1.0]])]});
            var Q1;
            {var subQ0=sQuery(id+"F12.wireOp",EDGE,"E49.2.0");Q1=makeQuery(id+"F12.imprint","IMPRINT",FACE,{"disambiguationData":[TD([[makeQuery(id+"F12.imprint","IMPRINT",EDGE,{"derivedFrom":subQ0}),-1.0]])]});}
            var Q2;
            {var subQ0=sQuery(id+"F12.wireOp",EDGE,"E49.1.0");Q2=makeQuery(id+"F12.imprint","IMPRINT",FACE,{"disambiguationData":[TD([[makeQuery(id+"F12.imprint","IMPRINT",EDGE,{"derivedFrom":subQ0}),-1.0]])]});}
            var Q3;
            {var subQ0=sQuery(id+"F12.wireOp",EDGE,"E47");Q3=makeQuery(id+"F12.imprint","IMPRINT",FACE,{"disambiguationData":[TD([[makeQuery(id+"F12.imprint","IMPRINT",EDGE,{"derivedFrom":subQ0}),-1.0]])]});}
            var Q4;
            {var subQ0=sQuery(id+"F12.wireOp",EDGE,"E50.1.4.0");Q4=makeQuery(id+"F12.imprint","IMPRINT",FACE,{"disambiguationData":[TD([[makeQuery(id+"F12.imprint","IMPRINT",EDGE,{"derivedFrom":subQ0}),-1.0]])]});}
            var Q5;
            {var subQ0=sQuery(id+"F12.wireOp",EDGE,"E50.1.3.0");Q5=makeQuery(id+"F12.imprint","IMPRINT",FACE,{"disambiguationData":[TD([[makeQuery(id+"F12.imprint","IMPRINT",EDGE,{"derivedFrom":subQ0}),-1.0]])]});}
            var Q6;
            {var subQ0=sQuery(id+"F12.wireOp",EDGE,"E46");var subQ5=makeQuery(id+"F12.imprint","INTERSECT",VERTEX,{"derivedFrom":[subQ0,sQuery(id+"F12.wireOp",EDGE,"E47")]});Q6=makeQuery(id+"F12.imprint","IMPRINT",FACE,{"disambiguationData":[TD([[makeQuery(id+"F12.imprint","IMPRINT",EDGE,{"disambiguationData":[TD([[subQ5,-1.0]])],"derivedFrom":subQ0}),1.0]])]});}
            var Q7;
            {var subQ0=sQuery(id+"F12.wireOp",EDGE,"E51.1.5.0");Q7=makeQuery(id+"F12.imprint","IMPRINT",FACE,{"disambiguationData":[TD([[makeQuery(id+"F12.imprint","IMPRINT",EDGE,{"derivedFrom":subQ0}),-1.0]])]});}
            var Q8;
            {var subQ0=sQuery(id+"F12.wireOp",EDGE,"E51.1.6.0");Q8=makeQuery(id+"F12.imprint","IMPRINT",FACE,{"disambiguationData":[TD([[makeQuery(id+"F12.imprint","IMPRINT",EDGE,{"derivedFrom":subQ0}),-1.0]])]});}
            extrude(context, id + "F14", {"entities" : qUnion([Q0, Q1, Q2, Q3, Q4, Q5, Q6, Q7, Q8]), "depth" : 10 * mm, "offsetDistance" : 25 * mm});
        }
        {
            var Q0;
            Q0=makeQuery(id+"F3.imprint","IMPRINT",FACE,{"disambiguationData":[TD([[makeQuery(id+"F3.imprint","IMPRINT",EDGE,{"derivedFrom":sQuery(id+"F3.wireOp",EDGE,"E30.0.4.0")}),1.0]])]});
            extrude(context, id + "F15", {"entities" : qUnion([Q0]), "depth" : 250 * mm, "offsetDistance" : 25 * mm});
        }
        {
            var Q0;
            Q0=makeQuery(id+"F3.imprint","IMPRINT",FACE,{"disambiguationData":[TD([[makeQuery(id+"F3.imprint","IMPRINT",EDGE,{"derivedFrom":sQuery(id+"F3.wireOp",EDGE,"E30.0.5.0")}),1.0]])]});
            extrude(context, id + "F16", {"entities" : qUnion([Q0]), "depth" : 247 * mm, "offsetDistance" : 25 * mm});
        }
        {
            var Q0;
            Q0=makeQuery(id+"F12.imprint","IMPRINT",FACE,{"disambiguationData":[TD([[makeQuery(id+"F12.imprint","IMPRINT",EDGE,{"derivedFrom":sQuery(id+"F12.wireOp",EDGE,"E52")}),1.0]])]});
            var Q1;
            Q1=makeQuery(id+"F12.imprint","IMPRINT",FACE,{"disambiguationData":[TD([[makeQuery(id+"F12.imprint","IMPRINT",EDGE,{"derivedFrom":sQuery(id+"F12.wireOp",EDGE,"E53")}),-1.0]])]});
            extrude(context, id + "F17", {"entities" : qUnion([Q0, Q1]), "depth" : 45 * mm, "offsetDistance" : 25 * mm, "symmetric" : true});
        }
        {
            var Q0;
            Q0=makeQuery(id+"F12.imprint","IMPRINT",FACE,{"disambiguationData":[TD([[makeQuery(id+"F12.imprint","IMPRINT",EDGE,{"derivedFrom":sQuery(id+"F12.wireOp",EDGE,"E52")}),1.0]])]});
            extrude(context, id + "F18", {"entities" : qUnion([Q0]), "operationType" : NewBodyOperationType.REMOVE, "depth" : 35 * mm, "offsetDistance" : 25 * mm, "symmetric" : true});
        }
        {
            var Q0;
            Q0=makeQuery(id+"F12.imprint","IMPRINT",FACE,{"disambiguationData":[TD([[makeQuery(id+"F12.imprint","IMPRINT",EDGE,{"derivedFrom":sQuery(id+"F12.wireOp",EDGE,"E52")}),1.0]])]});
            extrude(context, id + "F19", {"entities" : qUnion([Q0]), "operationType" : NewBodyOperationType.ADD, "depth" : (35 - 2 * 1.1) * mm, "offsetDistance" : 25 * mm, "symmetric" : true});
        }
        {
            var Q0;
            Q0=qCreatedBy(makeId("Top.planeOp"),FACE);
            var sketch = newSketch(context, id + "F20", { "sketchPlane" : qUnion([Q0])});
            skLineSegment(sketch, "E55.bottom", {"start": v(-28.85, -21.15) * mm, "end": v(-71.15, -21.15) * mm});
            skLineSegment(sketch, "E55.top", {"start": v(-28.85, 21.15) * mm, "end": v(-71.15, 21.15) * mm});
            skLineSegment(sketch, "E55.left", {"start": v(-28.85, -21.15) * mm, "end": v(-28.85, 21.15) * mm});
            skLineSegment(sketch, "E55.right", {"start": v(-71.15, -21.15) * mm, "end": v(-71.15, 21.15) * mm});
            skPoint(sketch, "E55.middle", {"position": v(-50, 0) * mm});
            skLineSegment(sketch, "E56.bottom", {"start": v(-34.5, -15.5) * mm, "end": v(-65.5, -15.5) * mm, "construction": true});
            skLineSegment(sketch, "E56.top", {"start": v(-34.5, 15.5) * mm, "end": v(-65.5, 15.5) * mm, "construction": true});
            skLineSegment(sketch, "E56.left", {"start": v(-34.5, -15.5) * mm, "end": v(-34.5, 15.5) * mm, "construction": true});
            skLineSegment(sketch, "E56.right", {"start": v(-65.5, -15.5) * mm, "end": v(-65.5, 15.5) * mm, "construction": true});
            skCircle(sketch, "E57", {"center": v(-34.5, 15.5) * mm, "radius": 1.5 * mm});
            skCircle(sketch, "E58", {"center": v(-34.5, -15.5) * mm, "radius": 1.5 * mm});
            skCircle(sketch, "E59", {"center": v(-65.5, -15.5) * mm, "radius": 1.5 * mm});
            skCircle(sketch, "E60", {"center": v(-65.5, 15.5) * mm, "radius": 1.5 * mm});
            skCircle(sketch, "E61", {"center": v(-50, 0) * mm, "radius": 11 * mm});
            skCircle(sketch, "E62", {"center": v(-50, 0) * mm, "radius": 2.5 * mm});
            skSolve(sketch);
        }
        {
            var Q0;
            Q0=makeQuery(id+"F20.imprint","IMPRINT",FACE,{"disambiguationData":[TD([[makeQuery(id+"F20.imprint","IMPRINT",EDGE,{"derivedFrom":sQuery(id+"F20.wireOp",EDGE,"E55.bottom")}),-1.0]])]});
            var Q1;
            Q1=makeQuery(id+"F20.imprint","IMPRINT",FACE,{"disambiguationData":[TD([[makeQuery(id+"F20.imprint","IMPRINT",EDGE,{"derivedFrom":sQuery(id+"F20.wireOp",EDGE,"E61")}),1.0]])]});
            var Q2;
            Q2=makeQuery(id+"F20.imprint","IMPRINT",FACE,{"disambiguationData":[TD([[makeQuery(id+"F20.imprint","IMPRINT",EDGE,{"derivedFrom":sQuery(id+"F20.wireOp",EDGE,"E62")}),1.0]])]});
            extrude(context, id + "F21", {"entities" : qUnion([Q0, Q1, Q2]), "oppositeDirection" : true, "depth" : 40 * mm, "offsetDistance" : 25 * mm});
        }
        {
            var Q0;
            Q0=makeQuery(id+"F20.imprint","IMPRINT",FACE,{"disambiguationData":[TD([[makeQuery(id+"F20.imprint","IMPRINT",EDGE,{"derivedFrom":sQuery(id+"F20.wireOp",EDGE,"E61")}),1.0]])]});
            extrude(context, id + "F22", {"entities" : qUnion([Q0]), "operationType" : NewBodyOperationType.ADD, "depth" : 2 * mm, "offsetDistance" : 25 * mm});
        }
        {
            var Q0;
            Q0=makeQuery(id+"F20.imprint","IMPRINT",FACE,{"disambiguationData":[TD([[makeQuery(id+"F20.imprint","IMPRINT",EDGE,{"derivedFrom":sQuery(id+"F20.wireOp",EDGE,"E62")}),1.0]])]});
            extrude(context, id + "F23", {"entities" : qUnion([Q0]), "operationType" : NewBodyOperationType.ADD, "depth" : (24 + 2) * mm, "offsetDistance" : 25 * mm});
        }
        {
            var Q0;
            Q0=makeQuery(id+"F20.imprint","IMPRINT",FACE,{"disambiguationData":[TD([[makeQuery(id+"F20.imprint","IMPRINT",EDGE,{"derivedFrom":sQuery(id+"F20.wireOp",EDGE,"E60")}),1.0]])]});
            var Q1;
            Q1=makeQuery(id+"F20.imprint","IMPRINT",FACE,{"disambiguationData":[TD([[makeQuery(id+"F20.imprint","IMPRINT",EDGE,{"derivedFrom":sQuery(id+"F20.wireOp",EDGE,"E57")}),1.0]])]});
            var Q2;
            Q2=makeQuery(id+"F20.imprint","IMPRINT",FACE,{"disambiguationData":[TD([[makeQuery(id+"F20.imprint","IMPRINT",EDGE,{"derivedFrom":sQuery(id+"F20.wireOp",EDGE,"E58")}),1.0]])]});
            var Q3;
            Q3=makeQuery(id+"F20.imprint","IMPRINT",FACE,{"disambiguationData":[TD([[makeQuery(id+"F20.imprint","IMPRINT",EDGE,{"derivedFrom":sQuery(id+"F20.wireOp",EDGE,"E59")}),1.0]])]});
            var Q4;
            Q4=makeQuery(id+"F21.opExtrude","CAP_FACE",FACE,{"disambiguationData":[OSD([sQuery(id+"F20.wireOp",EDGE,"E55.bottom"),sQuery(id+"F20.wireOp",EDGE,"E55.top"),sQuery(id+"F20.wireOp",EDGE,"E55.left"),sQuery(id+"F20.wireOp",EDGE,"E55.right"),sQuery(id+"F20.wireOp",EDGE,"E57"),sQuery(id+"F20.wireOp",EDGE,"E58"),sQuery(id+"F20.wireOp",EDGE,"E59"),sQuery(id+"F20.wireOp",EDGE,"E60")])],"isStart":false});
            extrude(context, id + "F24", {"entities" : qUnion([Q0, Q1, Q2, Q3]), "operationType" : NewBodyOperationType.ADD, "endBound" : BoundingType.UP_TO_SURFACE, "oppositeDirection" : true, "depth" : 25 * mm, "endBoundEntityFace" : qUnion([Q4]), "offsetDistance" : 8 * mm, "offsetOppositeDirection" : true, "hasSecondDirection" : true, "secondDirectionOppositeDirection" : true, "secondDirectionDepth" : 4.5 * mm});
        }
        {
            var Q0;
            Q0=makeQuery(id+"F21.opExtrude","SWEPT_EDGE",EDGE,{"disambiguationData":[OSD([sQuery(id+"F20.wireOp",EDGE,"E55.top"),sQuery(id+"F20.wireOp",EDGE,"E55.right")])]});
            var Q1;
            Q1=makeQuery(id+"F21.opExtrude","SWEPT_EDGE",EDGE,{"disambiguationData":[OSD([sQuery(id+"F20.wireOp",EDGE,"E55.bottom"),sQuery(id+"F20.wireOp",EDGE,"E55.right")])]});
            var Q2;
            Q2=makeQuery(id+"F21.opExtrude","SWEPT_EDGE",EDGE,{"disambiguationData":[OSD([sQuery(id+"F20.wireOp",EDGE,"E55.bottom"),sQuery(id+"F20.wireOp",EDGE,"E55.left")])]});
            var Q3;
            Q3=makeQuery(id+"F21.opExtrude","SWEPT_EDGE",EDGE,{"disambiguationData":[OSD([sQuery(id+"F20.wireOp",EDGE,"E55.top"),sQuery(id+"F20.wireOp",EDGE,"E55.left")])]});
            chamfer(context, id + "F25", {"entities" : qUnion([Q0, Q1, Q2, Q3]), "width" : 5 * mm, "tangentPropagation" : true});
        }
        {
            var Q0;
            Q0=qCreatedBy(makeId("Top.planeOp"),FACE);
            var sketch = newSketch(context, id + "F26", { "sketchPlane" : qUnion([Q0])});
            skLineSegment(sketch, "E63.bottom", {"start": v(507, -107) * mm, "end": v(193, -107) * mm});
            skLineSegment(sketch, "E63.top", {"start": v(507, 107) * mm, "end": v(193, 107) * mm});
            skLineSegment(sketch, "E63.left", {"start": v(507, -107) * mm, "end": v(507, 107) * mm});
            skLineSegment(sketch, "E63.right", {"start": v(193, -107) * mm, "end": v(193, 107) * mm});
            skPoint(sketch, "E63.middle", {"position": v(350, 0) * mm});
            skLineSegment(sketch, "E64.bottom", {"start": v(504.5, -104.5) * mm, "end": v(195.5, -104.5) * mm, "construction": true});
            skLineSegment(sketch, "E64.top", {"start": v(504.5, 104.5) * mm, "end": v(195.5, 104.5) * mm, "construction": true});
            skLineSegment(sketch, "E64.left", {"start": v(504.5, -104.5) * mm, "end": v(504.5, 104.5) * mm, "construction": true});
            skLineSegment(sketch, "E64.right", {"start": v(195.5, -104.5) * mm, "end": v(195.5, 104.5) * mm, "construction": true});
            skCircle(sketch, "E65", {"center": v(195.5, 104.5) * mm, "radius": 1.5 * mm});
            skCircle(sketch, "E66", {"center": v(504.5, 104.5) * mm, "radius": 1.5 * mm});
            skCircle(sketch, "E67", {"center": v(504.5, -104.5) * mm, "radius": 1.5 * mm});
            skCircle(sketch, "E68", {"center": v(195.5, -104.5) * mm, "radius": 1.5 * mm});
            skSolve(sketch);
        }
        {
            var Q0;
            Q0=makeQuery(id+"F26.imprint","IMPRINT",FACE,{"disambiguationData":[TD([[makeQuery(id+"F26.imprint","IMPRINT",EDGE,{"derivedFrom":sQuery(id+"F26.wireOp",EDGE,"E63.bottom")}),-1.0]])]});
            extrude(context, id + "F27", {"entities" : qUnion([Q0]), "depth" : 2 * mm, "offsetDistance" : 25 * mm});
        }
        {
            var Q0;
            Q0=qCreatedBy(makeId("Top.planeOp"),FACE);
            var sketch = newSketch(context, id + "F28", { "sketchPlane" : qUnion([Q0])});
            skLineSegment(sketch, "E69.bottom", {"start": v(501, 107) * mm, "end": v(199, 107) * mm});
            skLineSegment(sketch, "E69.top", {"start": v(501, -107) * mm, "end": v(199, -107) * mm});
            skLineSegment(sketch, "E69.left", {"start": v(501, 107) * mm, "end": v(501, -107) * mm});
            skLineSegment(sketch, "E69.right", {"start": v(199, 107) * mm, "end": v(199, -107) * mm});
            skPoint(sketch, "E69.middle", {"position": v(350, 0) * mm});
            skSolve(sketch);
        }
        {
            var Q0;
            Q0=makeQuery(id+"F28.imprint","IMPRINT",FACE,{"disambiguationData":[TD([[makeQuery(id+"F28.imprint","IMPRINT",EDGE,{"derivedFrom":sQuery(id+"F28.wireOp",EDGE,"E69.bottom")}),1.0]])]});
            extrude(context, id + "F29", {"entities" : qUnion([Q0]), "depth" : 3 * mm, "offsetDistance" : 25 * mm});
        }
    });
